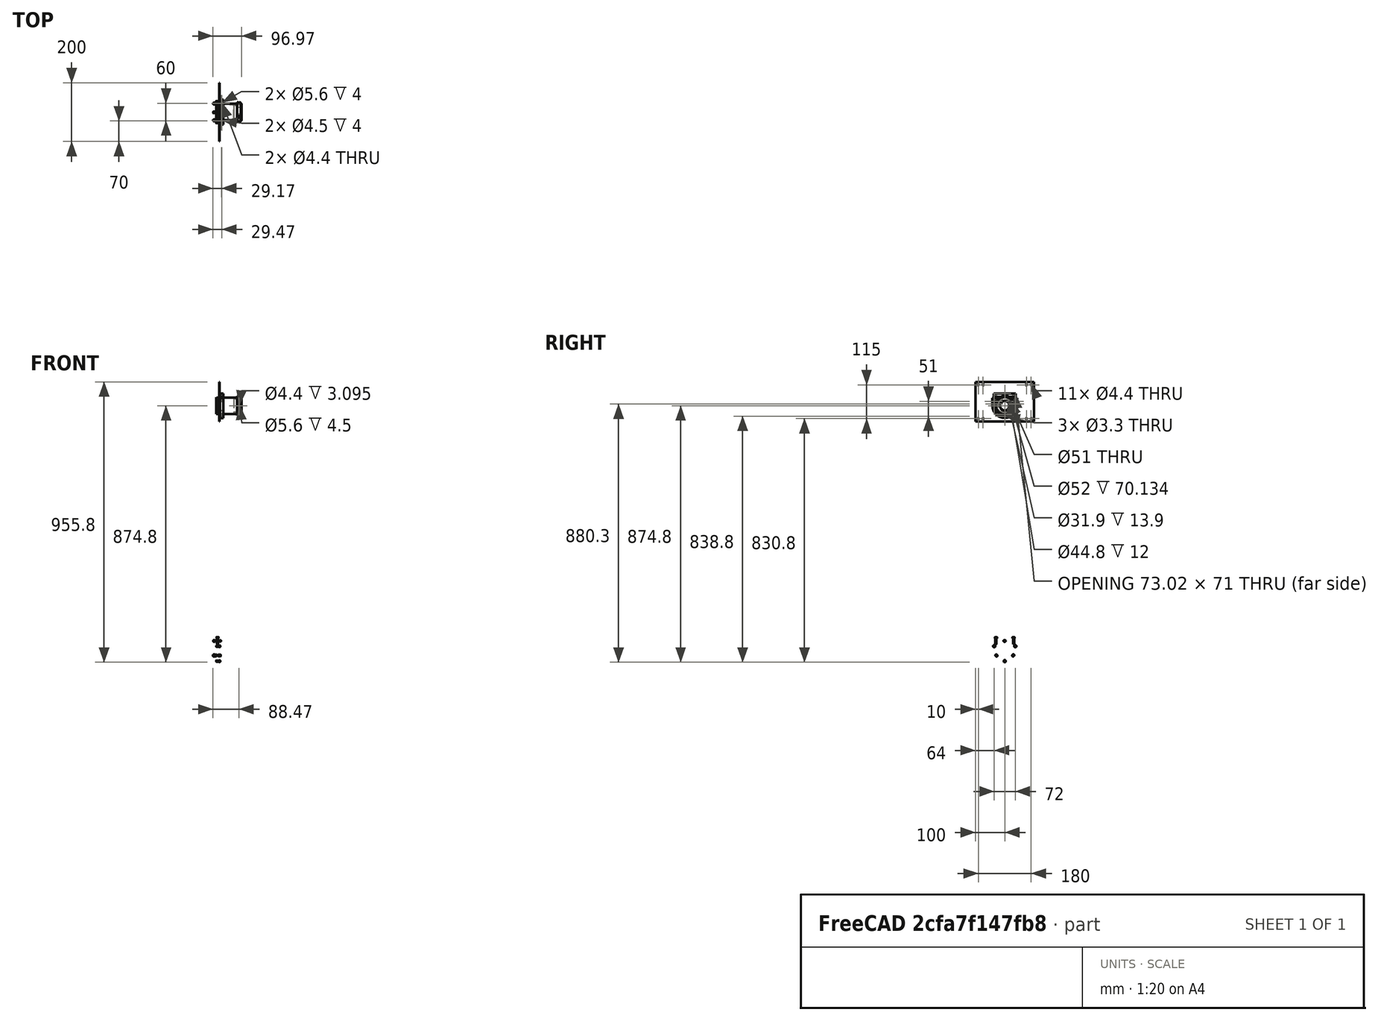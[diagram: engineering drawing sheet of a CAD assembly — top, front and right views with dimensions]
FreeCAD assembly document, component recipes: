
FREECAD ASSEMBLY — COMPONENT RECIPES ("Focuser")

This assembly document has 6 components, labeled P0..P5 below (a component is one placed body or linked part). 6 of them carry a construction recipe — the FreeCAD feature program that regenerates the part from scratch, quoted from this document or its linked companion documents; the rest are supplied as boundary geometry only. No exploded tour is included for this assembly.
COMPONENT P0 — recipe-attached ("FocuserTube", modeled in this document).
Construction recipe (the document's own serialized feature program — sketch geometry with constraints, then the solid features built on it; lengths are millimeters unless a unit is written):

FEATURE [Sketcher::SketchObject] Sketch022  label="Focuser_Profile"
  FullyConstrained = true
  MapMode = 5
  Support = -> [XY_Plane007]
  expr: Constraints[10] = <<Common>>#<<Parameters>>.foc_inner / 2
  expr: Constraints[11] = <<Common>>#<<Parameters>>.foc_flange
  expr: Constraints[16] = (<<Common>>#<<Parameters>>.foc_flangeinner + <<Common>>#<<Parameters>>.foc_itol) / 2
  expr: Constraints[18] = <<Common>>#<<Parameters>>.foc_shaft
  expr: Constraints[19] = <<Common>>#<<Parameters>>.foc_wall
  expr: Constraints[26] = <<Common>>#<<Parameters>>.foc_spacing / 2
  expr: Constraints[27] = <<Common>>#<<Parameters>>.foc_fheight
  sketch-geometry (12):
    g0: LineSegment StartX=0 StartY=26 StartZ=0 EndX=70.134 EndY=26 EndZ=0
    g1: LineSegment StartX=0 StartY=26 StartZ=0 EndX=0 EndY=29 EndZ=0
    g2: LineSegment StartX=2 StartY=28 StartZ=0 EndX=72 EndY=28 EndZ=0
    g3: LineSegment StartX=72 StartY=28 StartZ=0 EndX=72 EndY=33 EndZ=0
    g4: LineSegment StartX=72 StartY=33 StartZ=0 EndX=82 EndY=33 EndZ=0
    g5: LineSegment StartX=84 StartY=31 StartZ=0 EndX=84 EndY=25.5 EndZ=0
    g6: LineSegment StartX=70.134 StartY=26 StartZ=0 EndX=72 EndY=25.5 EndZ=0
    g7: LineSegment StartX=72 StartY=25.5 StartZ=0 EndX=84 EndY=25.5 EndZ=0
    g8: LineSegment StartX=0 StartY=29 StartZ=0 EndX=1 EndY=29 EndZ=0
    g9: LineSegment StartX=1 StartY=29 StartZ=0 EndX=2 EndY=28 EndZ=0
    g10: LineSegment StartX=72 StartY=28 StartZ=0 EndX=72 EndY=25.5 EndZ=0
    g11: ArcOfCircle CenterX=82 CenterY=31 CenterZ=0 NormalX=0 NormalY=0 NormalZ=1 AngleXU=0 Radius=2 StartAngle=4e-16 EndAngle=1.5708
  constraints (34):
    c: PointOnObject(g0,g-2)
    c: Horizontal(g0)
    c: Coincident(g1,g0)
    c: PointOnObject(g1,g-2)
    c: Horizontal(g2)
    c: Coincident(g3,g2)
    c: Vertical(g3)
    c: Coincident(g4,g3)
    c: Horizontal(g4)
    c: Vertical(g5)
    c: DistanceY(g-1,g0) = 26
    c: DistanceY(g0,g3) = 7
    c: Coincident(g6,g0)
    c: Coincident(g7,g6)
    c: Horizontal(g7)
    c: Coincident(g7,g5)
    c: DistanceY(g5) = 25.5
    c: Angle(g3,g6) = 1.309
    c: DistanceX(g1,g2) = 72
    c: DistanceY(g0,g2) = 2
    c: Coincident(g8,g1)
    c: Horizontal(g8)
    c: Coincident(g9,g8)
    c: Coincident(g9,g2)
    c: DistanceX(g8,g8) = 1
    c: Angle(g2,g9) = 2.35619
    c: DistanceY(g2,g1) = 1
    c: DistanceX(g6,g5) = 12
    c: Coincident(g10,g2)
    c: Coincident(g10,g6)
    c: Vertical(g10)
    c: Tangent(g4,g11) = 1.5708
    c: Tangent(g5,g11) = 1.5708
    c: Radius(g11) = 2
FEATURE [PartDesign::Revolution] Revolution001  label="Focuser_Shaft"
  Angle = 360
  Axis = (1,0,0)
  Base = (0,0,0)
  Profile = -> Sketch022
  ReferenceAxis = -> Sketch022 [H_Axis]
FEATURE [PartDesign::Plane] DatumPlane018  label="FocuserShaft_DatumPlane_Midpoint"
  AttachmentOffset = pos=(78,0,0) rot=(0,0,1;0rad)
  Length = 125.951
  MapMode = 5
  Placement = pos=(78,0,0) rot=(1,0,0;1.5708rad)
  ResizeMode = 0
  Support = -> [XZ_Plane007]
  Width = 82.8577
  expr: .AttachmentOffset.Base.x = <<Common>>#<<Parameters>>.foc_fheight / 2 + <<Common>>#<<Parameters>>.foc_shaft
FEATURE [Sketcher::SketchObject] Sketch031  label="FocuserShaft_Nut_Sketch"
  AttachmentOffset = pos=(0,0,33) rot=(0,0,1;0rad)
  FullyConstrained = true
  MapMode = 5
  Placement = pos=(78,33,7.3e-15) rot=(0,0.707107,0.707107;3.14159rad)
  Support = -> [DatumPlane018]
  expr: .AttachmentOffset.Base.z = <<Common>>#<<Parameters>>.foc_inner / 2 + <<Common>>#<<Parameters>>.foc_flange
  expr: Constraints[1] = <<Common>>#<<Parameters>>.acc_M4Bore
  sketch-geometry (1):
    g0: Circle CenterX=0 CenterY=0 CenterZ=0 NormalX=0 NormalY=0 NormalZ=1 AngleXU=0 Radius=2.8
  constraints (2):
    c: Coincident(g0,g-1)
    c: Diameter(g0) = 5.6
FEATURE [Sketcher::SketchObject] Sketch032  label="FocuserShaft_ScrewHole_Sketch"
  FullyConstrained = true
  MapMode = 5
  Placement = pos=(78,0,0) rot=(1,0,0;1.5708rad)
  Support = -> [DatumPlane018]
  sketch-geometry (1):
    g0: Circle CenterX=0 CenterY=0 CenterZ=0 NormalX=0 NormalY=0 NormalZ=1 AngleXU=0 Radius=2.2
  constraints (2):
    c: Coincident(g0,g-1)
    c: Diameter(g0) = 4.4
FEATURE [PartDesign::CoordinateSystem] Local_CS047  label="LCS_TubeBase"
  AttacherType = Attacher::AttachEngine3D
  MapMode = 11
  Placement = pos=(2,0,0) rot=(0.707107,0,0.707107;3.14159rad)
  Support = -> [Revolution001]
FEATURE [PartDesign::Plane] DatumPlane038  label="FocuserShaft_DatumPlane_AdaptorCut"
  AttachmentOffset = pos=(78,0,0) rot=(1,0,0;2.0944rad)
  Length = 128.821
  MapMode = 5
  Placement = pos=(78,0,0) rot=(1,0,0;3.66519rad)
  ResizeMode = 0
  Support = -> [XZ_Plane007]
  Width = 109.932
  expr: .AttachmentOffset.Base.x = <<Common>>#<<Parameters>>.foc_fheight / 2 + <<Common>>#<<Parameters>>.foc_shaft
FEATURE [Sketcher::SketchObject] Sketch146  label="FocuserShaft_AdaptorCut_Sketch"
  AttachmentOffset = pos=(0,0,-24.4) rot=(0,0,1;0rad)
  FullyConstrained = true
  MapMode = 5
  Placement = pos=(78,-12.2,21.131) rot=(1,0,0;3.66519rad)
  Support = -> [DatumPlane038]
  expr: .AttachmentOffset.Base.z = -(<<Common>>#<<Parameters>>.foc_flangeinner / 2) + 1
  expr: Constraints[13] = <<Common>>#<<Parameters>>.foc_fheight / 2 + 1
  expr: Constraints[5] = <<Common>>#<<Parameters>>.sec_sidebolt + 2
  sketch-geometry (5):
    g0: LineSegment StartX=7 StartY=3 StartZ=0 EndX=0 EndY=3 EndZ=0
    g1: LineSegment StartX=-6e-16 StartY=-3 StartZ=0 EndX=7 EndY=-3 EndZ=0
    g2: LineSegment StartX=7 StartY=-3 StartZ=0 EndX=7 EndY=3 EndZ=0
    g3: ArcOfCircle CenterX=0 CenterY=0 CenterZ=0 NormalX=0 NormalY=0 NormalZ=1 AngleXU=0 Radius=3 StartAngle=1.5708 EndAngle=4.71239
    g4: LineSegment StartX=-6e-16 StartY=3 StartZ=0 EndX=-6e-16 EndY=-3 EndZ=0
  constraints (15):
    c: Coincident(g1,g2)
    c: Coincident(g2,g0)
    c: Horizontal(g0)
    c: Horizontal(g1)
    c: Vertical(g2)
    c: DistanceY(g2,g2) = 6
    c: Symmetric(g0,g1,g-1)
    c: Coincident(g3,g0)
    c: Coincident(g3,g1)
    c: PointOnObject(g4,g0)
    c: Coincident(g4,g1)
    c: Vertical(g4)
    c: PointOnObject(g3,g4)
    c: DistanceX(g3,g0) = 7
    c: Coincident(g3,g-1)
FEATURE [PartDesign::CoordinateSystem] Local_CS229  label="LCS_TubeFlange"
  AttacherType = Attacher::AttachEngine3D
  MapMode = 11
  Placement = pos=(84,0,0) rot=(0.707107,0,0.707107;3.14159rad)
  Support = -> [Revolution001]
FEATURE [PartDesign::Pocket] Pocket195  label="FocuserShaft_Nut"
  BaseFeature = -> Revolution001
  Direction = (0,-1,-2e-16)
  Length = 4.5
  Length2 = 5
  Profile = -> Sketch031
  ReferenceAxis = -> Sketch031 [N_Axis]
  Type = 0
FEATURE [PartDesign::Pocket] Pocket196  label="FocuserShaft_ScrewHole"
  BaseFeature = -> Pocket195
  Direction = (0,1,2e-16)
  Length = 5
  Length2 = 5
  Profile = -> Sketch032
  ReferenceAxis = -> Sketch032 [N_Axis]
  Type = 1
FEATURE [PartDesign::PolarPattern] PolarPattern008  label="FocuserShaft_PolarPattern"
  Angle = 120
  Axis = -> X_Axis007
  BaseFeature = -> Pocket196
  Occurrences = 2
  Originals = -> [Pocket195,Pocket196]
  Reversed = true
FEATURE [PartDesign::CoordinateSystem] Local_CS048  label="LCS_TubeLock_Nut01"
  AttacherType = Attacher::AttachEngine3D
  AttachmentOffset = pos=(0,0,4) rot=(0,0,1;0rad)
  MapMode = 11
  Placement = pos=(78,32.5,6.8e-15) rot=(-0.57735,0.57735,0.57735;2.0944rad)
  Support = -> [PolarPattern008]
FEATURE [PartDesign::CoordinateSystem] Local_CS049  label="LCS_TubeLock_Nut02"
  AttacherType = Attacher::AttachEngine3D
  AttachmentOffset = pos=(0,0,4) rot=(0,0,1;0rad)
  MapMode = 11
  Placement = pos=(78,-16.25,-28.1458) rot=(0.694747,-0.694747,0.186157;2.77349rad)
  Support = -> [PolarPattern008]
FEATURE [PartDesign::CoordinateSystem] Local_CS050  label="LCS_TubeLock_Screw01"
  AttacherType = Attacher::AttachEngine3D
  AttachmentOffset = pos=(0,0,8) rot=(0,0,1;0rad)
  MapMode = 11
  Placement = pos=(78,36.5,7.2e-15) rot=(-0.57735,0.57735,0.57735;2.0944rad)
  Support = -> [PolarPattern008]
FEATURE [PartDesign::CoordinateSystem] Local_CS051  label="LCS_TubeLock_Screw02"
  AttacherType = Attacher::AttachEngine3D
  AttachmentOffset = pos=(0,0,8) rot=(0,0,1;0rad)
  MapMode = 11
  Placement = pos=(78,-18.25,-31.6099) rot=(0.694747,-0.694747,0.186157;2.77349rad)
  Support = -> [PolarPattern008]
FEATURE [PartDesign::Pocket] Pocket197  label="FocuserShaft_AdaptorCut"
  BaseFeature = -> PolarPattern008
  Direction = (0,-0.5,0.866025)
  Length = 5
  Length2 = 5
  Profile = -> Sketch146
  ReferenceAxis = -> Sketch146 [N_Axis]
  Type = 1
FEATURE [PartDesign::Chamfer] Chamfer001  label="FocuserShaft_RimChamfer"
  Angle = 45
  Base = -> Pocket197 [Edge14,Edge18]
  BaseFeature = -> Pocket197
  ChamferType = 0
  FlipDirection = false
  Size = 0.6
  Size2 = 1
  SupportTransform = false
  UseAllEdges = false
FEATURE [PartDesign::Body] Body007  label="FocuserTube"
  Group = -> [Sketch022,Revolution001,DatumPlane018,Sketch031,Sketch032,Local_CS047,Local_CS048,Local_CS049,Local_CS050,Local_CS051,DatumPlane038,Sketch146,Local_CS229,Pocket195,Pocket196,PolarPattern008,Pocket197,Chamfer001]
  Origin = -> Origin007
  Placement = pos=(110,0,835) rot=(0,0,1;0rad)
  Tip = -> Chamfer001
  expr: .Placement.Base.x = <<Common>>#<<Parameters>>.bolt_x + <<Common>>#<<Parameters>>.sec_poledia / 2 - <<Common>>#<<Parameters>>.foc_fheight
  expr: .Placement.Base.z = <<Common>>#<<Parameters>>.mirror_distance
COMPONENT P1 — recipe-attached ("FocuserSpring", modeled in this document).
Construction recipe (the document's own serialized feature program — sketch geometry with constraints, then the solid features built on it; lengths are millimeters unless a unit is written):

FEATURE [Sketcher::SketchObject] Sketch023  label="FocuserSpring_Base_Sketch"
  FullyConstrained = true
  MapMode = 5
  Placement = pos=(0,0,0) rot=(0.57735,0.57735,0.57735;2.0944rad)
  Support = -> [YZ_Plane008]
  expr: Constraints[13] = <<Common>>#<<Parameters>>.foc_clampblock
  expr: Constraints[2] = <<Common>>#<<Parameters>>.foc_baseflange
  expr: Constraints[3] = <<Common>>#<<Parameters>>.foc_inner / 2 + <<Common>>#<<Parameters>>.foc_wall + <<Common>>#<<Parameters>>.foc_spacing
  expr: Constraints[4] = <<Common>>#<<Parameters>>.foc_springblock
  expr: Constraints[9] = <<Common>>#<<Parameters>>.fbearing_outer + <<Common>>#<<Parameters>>.sec_fthick * 4
  sketch-geometry (6):
    g0: LineSegment StartX=38 StartY=42 StartZ=0 EndX=38 EndY=30 EndZ=0
    g1: LineSegment StartX=-38 StartY=30 StartZ=0 EndX=-38 EndY=42 EndZ=0
    g2: LineSegment StartX=-22 StartY=30 StartZ=0 EndX=22 EndY=30 EndZ=0
    g3: LineSegment StartX=-11 StartY=42 StartZ=0 EndX=11 EndY=42 EndZ=0
    g4: LineSegment StartX=-38 StartY=42 StartZ=0 EndX=38 EndY=42 EndZ=0
    g5: LineSegment StartX=-38 StartY=30 StartZ=0 EndX=38 EndY=30 EndZ=0
  constraints (17):
    c: Vertical(g0)
    c: Vertical(g1)
    c: DistanceY(g0,g0) = 12
    c: DistanceY(g-1,g0) = 30
    c: DistanceX(g1,g0) = 76
    c: Symmetric(g0,g1,g-2)
    c: Symmetric(g2,g2,g-2)
    c: Symmetric(g3,g3,g-2)
    c: Equal(g0,g1)
    c: DistanceX(g3,g3) = 22
    c: Coincident(g4,g1)
    c: Coincident(g4,g0)
    c: PointOnObject(g3,g4)
    c: DistanceX(g1,g2) = 16
    c: Coincident(g5,g1)
    c: Coincident(g5,g0)
    c: PointOnObject(g2,g5)
FEATURE [PartDesign::Pad] Pad007  label="FocuserSpring_Base"
  Direction = (1,-2e-16,3e-16)
  Length = 12
  Length2 = 100
  Placement = pos=(0,0,0) rot=(0.57735,0.57735,0.57735;2.0944rad)
  Profile = -> Sketch023
  Type = 0
  expr: Length = <<Common>>#<<Parameters>>.foc_fheight
FEATURE [Sketcher::SketchObject] Sketch065  label="FocuserSpring_Cut_Sketch"
  FullyConstrained = false
  MapMode = 5
  Support = -> [XY_Plane008]
  expr: Constraints[18] = <<Common>>#<<Parameters>>.fbearing_outer + <<Common>>#<<Parameters>>.sec_fthick
  expr: Constraints[1] = <<Common>>#<<Parameters>>.sec_sidebolt * 1.1
  expr: Constraints[28] = <<Common>>#<<Parameters>>.foc_fheight / 2
  expr: Constraints[2] = <<Common>>#<<Parameters>>.foc_springblock - <<Common>>#<<Parameters>>.foc_clampblock
  expr: Constraints[35] = <<Common>>#<<Parameters>>.fbearing_tilt
  expr: Constraints[4] = <<Common>>#<<Parameters>>.foc_fheight / 2
  sketch-geometry (14):
    g0: Circle CenterX=6 CenterY=30 CenterZ=0 NormalX=0 NormalY=0 NormalZ=1 AngleXU=0 Radius=2.2
    g1: Circle CenterX=6 CenterY=-30 CenterZ=0 NormalX=0 NormalY=0 NormalZ=1 AngleXU=0 Radius=2.2
    g2: GeomPoint X=6 Y=0 Z=0
    g3: LineSegment StartX=10.867 StartY=6.95063 StartZ=0 EndX=13 EndY=9.08366 EndZ=0
    g4: LineSegment StartX=13 StartY=9.08366 StartZ=0 EndX=13 EndY=-5.9999 EndZ=0
    g5: LineSegment StartX=13 StartY=-5.9999 StartZ=0 EndX=12 EndY=-5.9999 EndZ=0
    g6: LineSegment StartX=12 StartY=-5.9999 StartZ=0 EndX=10.867 EndY=6.95063 EndZ=0
    g7: LineSegment StartX=0 StartY=5.9999 StartZ=0 EndX=-1 EndY=5.9999 EndZ=0
    g8: LineSegment StartX=-1 StartY=5.9999 StartZ=0 EndX=-1 EndY=-9.08366 EndZ=0
    g9: LineSegment StartX=-1 StartY=-9.08366 StartZ=0 EndX=1.13302 EndY=-6.95063 EndZ=0
    g10: LineSegment StartX=1.13302 StartY=-6.95063 StartZ=0 EndX=0 EndY=5.9999 EndZ=0
    g11: LineSegment StartX=0.566512 StartY=-0.475369 StartZ=0 EndX=11.4335 EndY=0.475369 EndZ=0
    g12: GeomPoint X=0 Y=-8.08366 Z=0
    g13: GeomPoint X=12 Y=8.08366 Z=0
  constraints (36):
    c: Equal(g0,g1)
    c: Diameter(g1) = 4.4
    c: DistanceY(g1,g0) = 60
    c: Symmetric(g0,g1,g-1)
    c: DistanceX(g0) = 6
    c: Coincident(g3,g4)
    c: Coincident(g4,g5)
    c: Coincident(g5,g6)
    c: Coincident(g6,g3)
    c: Horizontal(g5)
    c: Vertical(g4)
    c: Coincident(g7,g8)
    c: Coincident(g8,g9)
    c: Coincident(g9,g10)
    c: Coincident(g10,g7)
    c: Horizontal(g7)
    c: Vertical(g8)
    c: Parallel(g9,g3)
    c: Distance(g6) = 13
    c: Equal(g6,g10)
    c: PointOnObject(g11,g10)
    c: PointOnObject(g11,g6)
    c: Symmetric(g5,g3,g11)
    c: Symmetric(g7,g9,g11)
    c: Equal(g7,g5)
    c: DistanceX(g5,g5) = 1
    c: PointOnObject(g2,g-1)
    c: PointOnObject(g2,g11)
    c: DistanceX(g-1,g2) = 6
    c: PointOnObject(g12,g9)
    c: PointOnObject(g13,g3)
    c: DistanceY(g12,g13) = 16.1673
    c: PointOnObject(g7,g-2)
    c: PointOnObject(g12,g-2)
    c: Angle(g9,g8) = 0.785398
    c: Angle(g-2,g10) = 0.0872665
FEATURE [PartDesign::Plane] DatumPlane008  label="FocuserSpring_DatumPlane_Shaft"
  AttachmentOffset = pos=(0,0,6) rot=(0,1,0;0.087266rad)
  Length = 94.7173
  MapMode = 2
  Placement = pos=(6,-1.3e-15,1.3e-15) rot=(0.543775,0.593426,0.593426;2.14549rad)
  ResizeMode = 0
  Support = -> [YZ_Plane008]
  Width = 81.6487
  expr: .AttachmentOffset.Base.z = <<Common>>#<<Parameters>>.foc_fheight / 2
  expr: .AttachmentOffset.Rotation.Pitch = <<Common>>#<<Parameters>>.fbearing_tilt
FEATURE [Sketcher::SketchObject] Sketch025  label="FocuserSpring_Shaft_Sketch"
  FullyConstrained = true
  MapMode = 5
  Placement = pos=(6,-1.4e-15,1.3e-15) rot=(0.543775,0.593426,0.593426;2.14549rad)
  Support = -> [DatumPlane008]
  expr: Constraints[0] = <<Common>>#<<Parameters>>.fbearing_inner * 1.1
  expr: Constraints[2] = <<Common>>#<<Parameters>>.foc_inner / 2 + <<Common>>#<<Parameters>>.foc_wall + <<Common>>#<<Parameters>>.fbearing_outer / 2
  sketch-geometry (1):
    g0: Circle CenterX=0 CenterY=33 CenterZ=0 NormalX=0 NormalY=0 NormalZ=1 AngleXU=0 Radius=1.65
  constraints (3):
    c: Diameter(g0) = 3.3
    c: PointOnObject(g0,g-2)
    c: DistanceY(g0) = 33
FEATURE [PartDesign::Pocket] Pocket021  label="FocuserSpring_Cut"
  BaseFeature = -> Pad007
  Direction = (0,0,-1)
  Length = 5
  Length2 = 100
  Midplane = true
  Placement = pos=(0,0,0) rot=(0.57735,0.57735,0.57735;2.0944rad)
  Profile = -> Sketch065
  Type = 1
FEATURE [PartDesign::Pocket] Pocket022  label="FocuserSpring_Shaft"
  BaseFeature = -> Pocket021
  Direction = (-0.996195,-0.0871557,-2e-16)
  Length = 5
  Length2 = 100
  Midplane = true
  Placement = pos=(0,0,0) rot=(0.57735,0.57735,0.57735;2.0944rad)
  Profile = -> Sketch025
  Type = 1
FEATURE [PartDesign::CoordinateSystem] Local_CS041  label="LCS_SpringBase_A"
  AttacherType = Attacher::AttachEngine3D
  MapMode = 11
  Placement = pos=(6,30,30) rot=(0,0,1;1.5708rad)
  Support = -> [Pocket022]
FEATURE [PartDesign::CoordinateSystem] Local_CS134  label="LCS_SpringBase_F"
  AttacherType = Attacher::AttachEngine3D
  MapMode = 11
  Placement = pos=(6,-30,30) rot=(0,0,1;1.5708rad)
  Support = -> [Pocket022]
FEATURE [PartDesign::CoordinateSystem] Local_CS043  label="LCS_SpringBolt_A"
  AttacherType = Attacher::AttachEngine3D
  MapMode = 11
  Placement = pos=(6,30,42) rot=(0,0,1;1.5708rad)
  Support = -> [Pocket022]
FEATURE [PartDesign::CoordinateSystem] Local_CS135  label="LCS_SpringBolt_F"
  AttacherType = Attacher::AttachEngine3D
  MapMode = 11
  Placement = pos=(6,-30,42) rot=(0,0,1;1.5708rad)
  Support = -> [Pocket022]
FEATURE [PartDesign::CoordinateSystem] Local_CS045  label="LCS_Bearing_Inner_Z"
  AttacherType = Attacher::AttachEngine3D
  MapMode = 11
  Placement = pos=(0.566512,-0.475369,33) rot=(0.70677,0.030858,-0.70677;3.0799rad)
  Support = -> [Pocket022]
FEATURE [PartDesign::CoordinateSystem] Local_CS046  label="LCS_Bearing_Outer_Z"
  AttacherType = Attacher::AttachEngine3D
  MapMode = 11
  Placement = pos=(11.4335,0.475369,33) rot=(0.70677,0.030858,0.70677;3.20329rad)
  Support = -> [Pocket022]
FEATURE [PartDesign::Chamfer] Chamfer004
  Angle = 45
  Base = -> Pocket022 [Face3,Face2]
  BaseFeature = -> Pocket022
  ChamferType = 0
  FlipDirection = false
  Placement = pos=(0,0,0) rot=(0.57735,0.57735,0.57735;2.0944rad)
  Size = 0.4
  Size2 = 1
  SupportTransform = false
  UseAllEdges = false
FEATURE [PartDesign::Body] Body008  label="FocuserSpring"
  Group = -> [Sketch023,Pad007,Sketch065,Pocket021,DatumPlane008,Sketch025,Pocket022,Local_CS041,Local_CS134,Local_CS043,Local_CS135,Local_CS045,Local_CS046,Chamfer004]
  Origin = -> Origin008
  Placement = pos=(122.7,0,835) rot=(0,0,1;0rad)
  Tip = -> Chamfer004
  expr: .Placement.Base.x = <<Common>>#<<Parameters>>.bolt_x + <<Common>>#<<Parameters>>.sec_poledia / 2 + <<Common>>#<<Parameters>>.sec_clamptol
  expr: .Placement.Base.z = <<Common>>#<<Parameters>>.mirror_distance
COMPONENT P2 — recipe-attached ("FocuserBase", modeled in this document).
Construction recipe (the document's own serialized feature program — sketch geometry with constraints, then the solid features built on it; lengths are millimeters unless a unit is written):

FEATURE [Sketcher::SketchObject] Sketch021  label="FocuserBase_Ring_Sketch"
  FullyConstrained = true
  MapMode = 5
  Placement = pos=(0,0,0) rot=(0.57735,0.57735,0.57735;2.0944rad)
  Support = -> [YZ_Plane057]
  expr: .Constraints.flange_inner = <<Common>>#<<Parameters>>.foc_inner / 2 + <<Common>>#<<Parameters>>.foc_wall + <<Common>>#<<Parameters>>.foc_spacing
  expr: .Constraints.flange_outer = .Constraints.flange_inner + <<Common>>#<<Parameters>>.foc_baseflange * 1 mm
  expr: Constraints[20] = <<Common>>#<<Parameters>>.foc_fthick * 1.5
  expr: Constraints[26] = max(<<Common>>#<<Parameters>>.foc_springblock * 1 mm; .Constraints.flange_outer * 2)
  expr: Constraints[30] = <<Common>>#<<Parameters>>.sec_fthick * 2
  sketch-geometry (14):
    g0: Circle CenterX=0 CenterY=0 CenterZ=0 NormalX=0 NormalY=0 NormalZ=1 AngleXU=0 Radius=30
    g1: Circle CenterX=0 CenterY=0 CenterZ=0 NormalX=0 NormalY=0 NormalZ=1 AngleXU=0 Radius=42
    g2: LineSegment StartX=0 StartY=0 StartZ=0 EndX=36.3731 EndY=-21 EndZ=0
    g3: LineSegment StartX=0 StartY=0 StartZ=0 EndX=-36.3731 EndY=-21 EndZ=0
    g4: LineSegment StartX=-42 StartY=26.25 StartZ=0 EndX=-22.1345 EndY=26.25 EndZ=0
    g5: LineSegment StartX=22.1345 StartY=26.25 StartZ=0 EndX=42 EndY=26.25 EndZ=0
    g6: LineSegment StartX=-42 StartY=26.25 StartZ=0 EndX=-42 EndY=8.27963e-05 EndZ=0
    g7: LineSegment StartX=-22.1345 StartY=26.25 StartZ=0 EndX=-22.1345 EndY=20.25 EndZ=0
    g8: LineSegment StartX=22.1345 StartY=26.25 StartZ=0 EndX=22.1345 EndY=20.25 EndZ=0
    g9: LineSegment StartX=42 StartY=26.25 StartZ=0 EndX=42 EndY=8.27947e-05 EndZ=0
    g10: GeomPoint X=0 Y=30 Z=0
    g11: ArcOfCircle CenterX=0 CenterY=0 CenterZ=0 NormalX=0 NormalY=0 NormalZ=1 AngleXU=0 Radius=30 StartAngle=2.40063 EndAngle=7.02415
    g12: ArcOfCircle CenterX=0 CenterY=0 CenterZ=0 NormalX=0 NormalY=0 NormalZ=1 AngleXU=0 Radius=42 StartAngle=3.14159 EndAngle=4.71239
    g13: ArcOfCircle CenterX=0 CenterY=0 CenterZ=0 NormalX=0 NormalY=0 NormalZ=1 AngleXU=0 Radius=42 StartAngle=4.71239 EndAngle=6.28319
  constraints (37):
    c: Coincident(g0,g-1)
    c: Coincident(g1,g0)
    c: Radius(g0) = 30  'flange_inner'
    c: Radius(g1) = 42  'flange_outer'
    c: Coincident(g2,g0)
    c: Coincident(g3,g0)
    c: PointOnObject(g2,g1)
    c: Angle(g3,g2) = 2.0944
    c: Horizontal(g4)
    c: Horizontal(g5)
    c: Coincident(g6,g4)
    c: Coincident(g7,g4)
    c: Vertical(g7)
    c: Coincident(g8,g5)
    c: Vertical(g8)
    c: Coincident(g9,g5)
    c: Symmetric(g4,g5,g-2)
    c: Equal(g4,g5)
    c: PointOnObject(g10,g0)
    c: PointOnObject(g10,g-2)
    c: DistanceY(g4,g10) = 3.75
    c: Coincident(g11,g-1)
    c: Coincident(g12,g11)
    c: Coincident(g12,g6)
    c: Coincident(g13,g11)
    c: Coincident(g13,g9)
    c: DistanceX(g4,g5) = 84
    c: Equal(g12,g1)
    c: Tangent(g6,g12)
    c: Tangent(g9,g13)
    c: DistanceY(g7,g7) = 6
    c: Coincident(g11,g7)
    c: Coincident(g11,g8)
    c: PointOnObject(g7,g0)
    c: Coincident(g13,g12)
    c: PointOnObject(g12,g-2)
    c: Symmetric(g3,g2,g-2)
FEATURE [PartDesign::Pad] Pad006  label="FocuserBase_Ring"
  Direction = (1,-2e-16,3e-16)
  Length = 12
  Length2 = 100
  Placement = pos=(0,0,0) rot=(0.57735,0.57735,0.57735;2.0944rad)
  Profile = -> Sketch021
  Type = 0
  expr: Length = <<Common>>#<<Parameters>>.foc_fheight
FEATURE [PartDesign::Plane] DatumPlane015  label="FocuserBase_DatumPlane_SideCut"
  AttachmentOffset = pos=(6,28.5788,-16.5) rot=(1,0,0;1.0472rad)
  Length = 64.2201
  MapMode = 2
  Placement = pos=(6,28.5788,-16.5) rot=(1,0,0;1.0472rad)
  ResizeMode = 0
  Support = -> [XY_Plane057]
  Width = 115.326
  expr: .AttachmentOffset.Base.x = <<Common>>#<<Parameters>>.foc_fheight / 2
  expr: .AttachmentOffset.Base.y = (<<Common>>#<<Parameters>>.foc_inner / 2 + <<Common>>#<<Parameters>>.foc_wall + <<Common>>#<<Parameters>>.fbearing_outer / 2) * sin(60)
  expr: .AttachmentOffset.Base.z = -(<<Common>>#<<Parameters>>.foc_inner / 2 + <<Common>>#<<Parameters>>.foc_wall + <<Common>>#<<Parameters>>.fbearing_outer / 2) * cos(60)
FEATURE [PartDesign::Plane] DatumPlane016  label="FocuserBase_DatumPlane_SideShaft"
  AttachmentOffset = pos=(0,0,0) rot=(0,-1,0;0.087266rad)
  Length = 126.274
  MapMode = 4
  Placement = pos=(6,28.5788,-16.5) rot=(0.725486,0.178129,0.664786;2.75759rad)
  ResizeMode = 0
  Support = -> [DatumPlane015]
  Width = 128.065
  expr: .AttachmentOffset.Rotation.Pitch = -<<Common>>#<<Parameters>>.fbearing_tilt
FEATURE [PartDesign::Plane] DatumPlane011  label="FocuserBase_DatumPlane_SpringShaft"
  AttachmentOffset = pos=(6,0,26.25) rot=(0,0,1;0rad)
  Length = 62.9615
  MapMode = 5
  Placement = pos=(6,0,26.25) rot=(0,0,1;0rad)
  ResizeMode = 0
  Support = -> [XY_Plane057]
  Width = 96.9615
  expr: .AttachmentOffset.Base.x = <<Common>>#<<Parameters>>.foc_fheight / 2
  expr: .AttachmentOffset.Base.z = <<Common>>#<<Parameters>>.foc_inner / 2 + <<Common>>#<<Parameters>>.foc_wall + <<Common>>#<<Parameters>>.foc_spacing - <<Common>>#<<Parameters>>.foc_fthick * 1.5
FEATURE [Sketcher::SketchObject] Sketch067  label="FocuserBase_SpringShaft_Sketch"
  FullyConstrained = true
  MapMode = 5
  Placement = pos=(6,0,26.25) rot=(0,0,1;0rad)
  Support = -> [DatumPlane011]
  expr: Constraints[0] = <<Common>>#<<Parameters>>.sec_sidebolt * 1.1
  expr: Constraints[3] = <<Common>>#<<Parameters>>.foc_springblock - <<Common>>#<<Parameters>>.foc_clampblock
  sketch-geometry (2):
    g0: Circle CenterX=0 CenterY=30 CenterZ=0 NormalX=0 NormalY=0 NormalZ=1 AngleXU=0 Radius=2.2
    g1: Circle CenterX=0 CenterY=-30 CenterZ=0 NormalX=0 NormalY=0 NormalZ=1 AngleXU=0 Radius=2.2
  constraints (5):
    c: Diameter(g1) = 4.4
    c: Equal(g1,g0)
    c: Symmetric(g1,g0,g-1)
    c: DistanceY(g1,g0) = 60
    c: PointOnObject(g0,g-2)
FEATURE [PartDesign::Plane] DatumPlane017  label="FocuserBase_DatumPlane_FrontFace"
  AttachmentOffset = pos=(0,0,12) rot=(0,0,1;0rad)
  Length = 99.1433
  MapMode = 5
  Placement = pos=(12,-2.7e-15,2.7e-15) rot=(0.57735,0.57735,0.57735;2.0944rad)
  ResizeMode = 0
  Support = -> [YZ_Plane057]
  Width = 83.3933
  expr: .AttachmentOffset.Base.z = <<Common>>#<<Parameters>>.foc_fheight
FEATURE [PartDesign::CoordinateSystem] Local_CS130  label="LCS_TubeDatum"
  AttacherType = Attacher::AttachEngine3D
  AttachmentOffset = pos=(0,0,-12) rot=(0,0,1;0rad)
  MapMode = 5
  Placement = pos=(-12,2.7e-15,-2.7e-15) rot=(0.57735,0.57735,0.57735;2.0944rad)
  Support = -> [YZ_Plane057]
  expr: .AttachmentOffset.Base.z = -<<Common>>#<<Parameters>>.foc_fheight
FEATURE [Sketcher::SketchObject] Sketch077  label="FocuserBase_MountHoles_Sketch"
  FullyConstrained = true
  MapMode = 5
  Placement = pos=(12,-2.7e-15,2.7e-15) rot=(0.57735,0.57735,0.57735;2.0944rad)
  Support = -> [DatumPlane017]
  expr: Constraints[2] = <<Common>>#<<Parameters>>.sec_collbolt
  expr: Constraints[5] = <<Common>>#<<Parameters>>.foc_mbrad
  expr: Constraints[6] = <<Common>>#<<Parameters>>.foc_mbrad - <<Common>>#<<Parameters>>.foc_baseflange / 2 - <<Common>>#<<Parameters>>.sec_fthick - <<Common>>#<<Parameters>>.sec_sidebolt * 3
  expr: Constraints[7] = <<Common>>#<<Parameters>>.foc_mbrad
  sketch-geometry (3):
    g0: Circle CenterX=0 CenterY=-36 CenterZ=0 NormalX=0 NormalY=0 NormalZ=1 AngleXU=0 Radius=2
    g1: Circle CenterX=-36 CenterY=15 CenterZ=0 NormalX=0 NormalY=0 NormalZ=1 AngleXU=0 Radius=2
    g2: Circle CenterX=36 CenterY=15 CenterZ=0 NormalX=0 NormalY=0 NormalZ=1 AngleXU=0 Radius=2
  constraints (8):
    c: Symmetric(g1,g2,g-2)
    c: PointOnObject(g0,g-2)
    c: Diameter(g0) = 4
    c: Equal(g0,g1)
    c: Equal(g0,g2)
    c: DistanceY(g0,g-1) = 36
    c: DistanceY(g2) = 15
    c: DistanceX(g2) = 36
FEATURE [PartDesign::CoordinateSystem] Local_CS137  label="LCS_FocuserBase_MountN"
  AttacherType = Attacher::AttachEngine3D
  AttachmentOffset = pos=(0,-36,0) rot=(0,0,1;1.5708rad)
  MapMode = 5
  Placement = pos=(12,-6.7e-15,-36) rot=(0.707107,0,0.707107;3.14159rad)
  Support = -> [DatumPlane017]
  expr: .AttachmentOffset.Base.y = -<<Common>>#<<Parameters>>.foc_mbrad
FEATURE [PartDesign::Plane] DatumPlane027  label="FocuserBase_DatumPlane_NutCut"
  AttachmentOffset = pos=(0,0,-3) rot=(0,0,1;0rad)
  Length = 62.9615
  MapMode = 2
  Placement = pos=(6,0,23.25) rot=(0,0,1;0rad)
  ResizeMode = 0
  Support = -> [DatumPlane011]
  Width = 96.9615
  expr: .AttachmentOffset.Base.z = -<<Common>>#<<Parameters>>.sec_fthick
FEATURE [PartDesign::Line] DatumLine002  label="FocuserBase_DatumLine_SideShaft"
  AttacherType = Attacher::AttachEngineLine
  Length = 20
  MapMode = 18
  Placement = pos=(6,28.5788,-16.5) rot=(0.725486,0.178129,0.664786;2.75759rad)
  ResizeMode = 0
  Support = -> [DatumPlane016]
FEATURE [Sketcher::SketchObject] Sketch066  label="FocuserBase_SideCut_Sketch"
  ExternalGeometry = -> [Pad006,DatumLine002]
  FullyConstrained = true
  MapMode = 5
  Placement = pos=(6,28.5788,-16.5) rot=(1,0,0;1.0472rad)
  Support = -> [DatumPlane015]
  expr: Constraints[37] = (<<Common>>#<<Parameters>>.fbearing_outer + <<Common>>#<<Parameters>>.foc_fthick) / 2
  expr: Constraints[38] = <<Common>>#<<Parameters>>.fbearing_inner / 2
  sketch-geometry (21):
    g0: LineSegment StartX=-6.4 StartY=8.92025 StartZ=0 EndX=-7.12588 EndY=0.623433 EndZ=0
    g1: LineSegment StartX=5.6 StartY=5.78394 StartZ=0 EndX=7.85175 EndY=7.67338 EndZ=0
    g2: LineSegment StartX=7.85175 StartY=7.67338 StartZ=0 EndX=7.12588 EndY=-0.623433 EndZ=0
    g3: LineSegment StartX=-4.51055 StartY=6.6685 StartZ=0 EndX=5.6 EndY=5.78394 EndZ=0
    g4: LineSegment StartX=-6.4 StartY=8.92025 StartZ=0 EndX=-4.51055 EndY=6.6685 EndZ=0
    g5: LineSegment StartX=-4.92454 StartY=1.93657 StartZ=0 EndX=-4.51055 EndY=6.6685 EndZ=0
    g6: LineSegment StartX=5.18601 StartY=1.05201 StartZ=0 EndX=5.6 EndY=5.78394 EndZ=0
    g7: LineSegment StartX=4.51055 StartY=-6.6685 StartZ=0 EndX=6.4 EndY=-8.92025 EndZ=0
    g8: LineSegment StartX=-5.6 StartY=-5.78394 StartZ=0 EndX=4.51055 EndY=-6.6685 EndZ=0
    g9: LineSegment StartX=-4.92454 StartY=1.93657 StartZ=0 EndX=5.18601 EndY=1.05201 EndZ=0
    g10: LineSegment StartX=-7.12588 StartY=0.623433 StartZ=0 EndX=7.12588 EndY=-0.623433 EndZ=0
    g11: LineSegment StartX=-5.05528 StartY=0.442279 StartZ=0 EndX=-5.6 EndY=-5.78394 EndZ=0
    g12: LineSegment StartX=-5.05528 StartY=0.442279 StartZ=0 EndX=-4.92454 EndY=1.93657 EndZ=0
    g13: LineSegment StartX=7.12588 StartY=-0.623433 StartZ=0 EndX=6.4 EndY=-8.92025 EndZ=0
    g14: LineSegment StartX=-7.12588 StartY=0.623433 StartZ=0 EndX=-7.85175 EndY=-7.67338 EndZ=0
    g15: LineSegment StartX=-7.85175 StartY=-7.67338 StartZ=0 EndX=-5.6 EndY=-5.78394 EndZ=0
    g16: LineSegment StartX=5.6 StartY=5.78394 StartZ=0 EndX=6 EndY=5.78394 EndZ=0
    g17: LineSegment StartX=-6.4 StartY=8.92025 StartZ=0 EndX=-6 EndY=8.92025 EndZ=0
    g18: LineSegment StartX=-6 StartY=-5.78394 StartZ=0 EndX=-5.6 EndY=-5.78394 EndZ=0
    g19: LineSegment StartX=6.4 StartY=-8.92025 StartZ=0 EndX=6 EndY=-8.92025 EndZ=0
    g20: LineSegment StartX=5.18601 StartY=1.05201 StartZ=0 EndX=4.51055 EndY=-6.6685 EndZ=0
  constraints (59):
    c: Coincident(g4,g0)
    c: Parallel(g3,g-5)
    c: Coincident(g5,g4)
    c: Coincident(g5,g3)
    c: Coincident(g6,g1)
    c: Coincident(g6,g3)
    c: Coincident(g1,g2)
    c: Parallel(g5,g0)
    c: Parallel(g6,g2)
    c: Angle(g4,g5) = 2.35619
    c: Parallel(g8,g-5)
    c: Perpendicular(g-5,g0)
    c: Angle(g6,g1) = 2.35619
    c: Parallel(g5,g6)
    c: Equal(g5,g6)
    c: Coincident(g9,g5)
    c: Coincident(g9,g6)
    c: Coincident(g10,g0)
    c: Coincident(g10,g2)
    c: PointOnObject(g0,g-5)
    c: PointOnObject(g2,g-5)
    c: PointOnObject(g11,g10)
    c: Coincident(g11,g8)
    c: Coincident(g12,g11)
    c: Coincident(g12,g5)
    c: Coincident(g13,g2)
    c: Coincident(g13,g7)
    c: Coincident(g7,g8)
    c: PointOnObject(g11,g5)
    c: Equal(g13,g2)
    c: Equal(g2,g0)
    c: Coincident(g14,g0)
    c: Coincident(g15,g14)
    c: Coincident(g15,g8)
    c: PointOnObject(g14,g0)
    c: Parallel(g15,g1)
    c: Parallel(g7,g4)
    c: Distance(g11) = 6.25
    c: Distance(g12) = 1.5
    c: Coincident(g16,g1)
    c: PointOnObject(g16,g-3)
    c: Horizontal(g16)
    c: Coincident(g17,g0)
    c: PointOnObject(g17,g-4)
    c: Horizontal(g17)
    c: PointOnObject(g18,g-4)
    c: Coincident(g18,g8)
    c: Horizontal(g18)
    c: Coincident(g19,g7)
    c: PointOnObject(g19,g-3)
    c: Horizontal(g19)
    c: Equal(g19,g16)
    c: Equal(g16,g17)
    c: Equal(g17,g18)
    c: Parallel(g11,g12)
    c: Coincident(g20,g6)
    c: Coincident(g20,g7)
    c: Parallel(g20,g6)
    c: DistanceX(g17,g17) = 0.4
FEATURE [PartDesign::Groove] Groove  label="FocuserBase_SideCut"
  Angle = 360
  Axis = (0.996195,-0.0435779,-0.0754791)
  Base = (6,28.5788,-16.5)
  BaseFeature = -> Pad006
  Placement = pos=(0,0,0) rot=(0.57735,0.57735,0.57735;2.0944rad)
  Profile = -> Sketch066
  ReferenceAxis = -> DatumLine002
FEATURE [PartDesign::PolarPattern] PolarPattern  label="FocuserBase_PolarPattern"
  Angle = 360
  Axis = -> X_Axis057
  BaseFeature = -> Groove
  Occurrences = 3
  Originals = -> [Groove]
  Placement = pos=(0,0,0) rot=(0.57735,0.57735,0.57735;2.0944rad)
FEATURE [PartDesign::CoordinateSystem] Local_CS033  label="LCS_Bearing_Inner_NF"
  AttacherType = Attacher::AttachEngine3D
  MapMode = 11
  Placement = pos=(0.944723,-28.3577,-16.883) rot=(0.663579,-0.401957,-0.630947;2.47638rad)
  Support = -> [PolarPattern]
FEATURE [PartDesign::CoordinateSystem] Local_CS034  label="LCS_Bearing_Inner_NA"
  AttacherType = Attacher::AttachEngine3D
  MapMode = 11
  Placement = pos=(0.944723,28.8,-16.117) rot=(-0.644711,-0.352973,0.678055;2.36216rad)
  Support = -> [PolarPattern]
FEATURE [PartDesign::CoordinateSystem] Local_CS035  label="LCS_Bearing_Outer_NF"
  AttacherType = Attacher::AttachEngine3D
  MapMode = 11
  Placement = pos=(11.0553,-28.8,-16.117) rot=(0.644711,0.352973,0.678055;2.36216rad)
  Support = -> [PolarPattern]
FEATURE [PartDesign::CoordinateSystem] Local_CS036  label="LCS_Bearing_Outer_NA"
  AttacherType = Attacher::AttachEngine3D
  MapMode = 11
  Placement = pos=(11.0553,28.3577,-16.883) rot=(0.663579,-0.401957,0.630947;3.8068rad)
  Support = -> [PolarPattern]
FEATURE [PartDesign::Hole] Hole  label="FocuserBase_SpringShaft"
  BaseFeature = -> PolarPattern
  CustomThreadClearance = 0
  Depth = 8
  DepthType = 0
  Diameter = 4.5
  DrillForDepth = false
  DrillPoint = 1
  DrillPointAngle = 118
  HoleCutCountersinkAngle = 90
  HoleCutCustomValues = false
  HoleCutDepth = 4
  HoleCutDiameter = 5.6
  HoleCutType = 1
  ModelThread = false
  Placement = pos=(0,0,0) rot=(0.57735,0.57735,0.57735;2.0944rad)
  Profile = -> Sketch067
  Tapered = false
  TaperedAngle = 90
  ThreadClass = 0
  ThreadDepth = 8
  ThreadDepthType = 0
  ThreadDirection = 0
  ThreadFit = 0
  ThreadSize = 11
  ThreadType = 1
  Threaded = false
  UseCustomThreadClearance = false
  expr: HoleCutDiameter = Common#<<Parameters>>.acc_M4Bore
FEATURE [PartDesign::CoordinateSystem] Local_CS037  label="LCS_SpringNut_F"
  AttacherType = Attacher::AttachEngine3D
  MapMode = 11
  Placement = pos=(6,-30,26.25) rot=(0,0,1;3.14159rad)
  Support = -> [Hole]
FEATURE [PartDesign::CoordinateSystem] Local_CS038  label="LCS_SpringNut_A"
  AttacherType = Attacher::AttachEngine3D
  MapMode = 11
  Placement = pos=(6,30,26.25) rot=(0,0,1;3.14159rad)
  Support = -> [Hole]
FEATURE [PartDesign::CoordinateSystem] Local_CS132  label="LCS_SpringAttachment_F"
  AttacherType = Attacher::AttachEngine3D
  AttachmentOffset = pos=(0,0,3.75) rot=(0,0,1;0rad)
  MapMode = 11
  Placement = pos=(6,-30,30) rot=(0,0,1;3.14159rad)
  Support = -> [Hole]
  expr: .AttachmentOffset.Base.z = <<Common>>#<<Parameters>>.foc_fthick * 1.5
FEATURE [PartDesign::CoordinateSystem] Local_CS133  label="LCS_SpringAttachment_A"
  AttacherType = Attacher::AttachEngine3D
  AttachmentOffset = pos=(0,0,3.75) rot=(0,0,1;0rad)
  MapMode = 11
  Placement = pos=(6,30,30) rot=(0,0,1;3.14159rad)
  Support = -> [Hole]
  expr: .AttachmentOffset.Base.z = <<Common>>#<<Parameters>>.foc_fthick * 1.5
FEATURE [PartDesign::Hole] Hole051  label="FocuserBase_MountHoles"
  BaseFeature = -> Hole
  CustomThreadClearance = 0
  Depth = 219.967
  DepthType = 1
  Diameter = 3.3
  DrillForDepth = false
  DrillPoint = 1
  DrillPointAngle = 118
  HoleCutCountersinkAngle = 90
  HoleCutCustomValues = false
  HoleCutDepth = 0
  HoleCutDiameter = 6.1
  HoleCutType = 0
  ModelThread = false
  Placement = pos=(0,0,0) rot=(0.57735,0.57735,0.57735;2.0944rad)
  Profile = -> Sketch077
  Tapered = false
  TaperedAngle = 90
  ThreadClass = 0
  ThreadDepth = 219.967
  ThreadDepthType = 0
  ThreadDirection = 0
  ThreadFit = 0
  ThreadSize = 11
  ThreadType = 1
  Threaded = true
  UseCustomThreadClearance = false
FEATURE [PartDesign::Chamfer] Chamfer  label="FocuserBase_Chamfer"
  Angle = 45
  Base = -> Hole051 [Face5,Face4]
  BaseFeature = -> Hole051
  ChamferType = 0
  FlipDirection = false
  Placement = pos=(0,0,0) rot=(0.57735,0.57735,0.57735;2.0944rad)
  Size = 0.4
  Size2 = 1
  SupportTransform = false
  UseAllEdges = false
FEATURE [PartDesign::Body] Body022004  label="FocuserBase"
  Group = -> [Sketch021,Pad006,DatumPlane015,Sketch066,DatumPlane016,DatumPlane011,Sketch067,DatumPlane017,Local_CS130,Local_CS033,Local_CS034,Local_CS035,Local_CS036,Local_CS037,Local_CS038,Local_CS132,Local_CS133,Sketch077,Local_CS137,DatumPlane027,DatumLine002,Groove,PolarPattern,Hole,Hole051,Chamfer]
  Origin = -> Origin057
  Placement = pos=(123,0,835) rot=(0,0,1;0rad)
  Tip = -> Chamfer
  expr: .Placement.Base.x = <<Common>>#<<Parameters>>.bolt_x + <<Common>>#<<Parameters>>.sec_poledia / 2 + <<Common>>#<<Parameters>>.sec_spthick
  expr: .Placement.Base.z = <<Common>>#<<Parameters>>.mirror_distance
COMPONENT P3 — recipe-attached ("FocuserPlate", modeled in this document).
Construction recipe (the document's own serialized feature program — sketch geometry with constraints, then the solid features built on it; lengths are millimeters unless a unit is written):

FEATURE [Sketcher::SketchObject] Sketch078  label="FocuserPlate_Sketch"
  FullyConstrained = true
  MapMode = 5
  Placement = pos=(0,0,0) rot=(0.57735,0.57735,0.57735;2.0944rad)
  Support = -> [YZ_Plane014]
  expr: Constraints[106] = <<Common>>#<<Parameters>>.sec_sidebolt_y
  expr: Constraints[107] = <<Common>>#<<Parameters>>.sec_sidebolt * 4
  expr: Constraints[111] = <<Common>>#<<Parameters>>.sec_sidebolt * 1.1
  expr: Constraints[11] = <<Common>>#<<Parameters>>.foc_inner / 2 + <<Common>>#<<Parameters>>.foc_wall + <<Common>>#<<Parameters>>.foc_spacing
  expr: Constraints[12] = -(<<Common>>#<<Parameters>>.sec_sidebolt_lower_z - <<Common>>#<<Parameters>>.mirror_distance) + <<Common>>#<<Parameters>>.sec_clampheight / 2
  expr: Constraints[151] = <<Common>>#<<Parameters>>.sec_sidebolt * 1.1
  expr: Constraints[153] = <<Common>>#<<Parameters>>.sec_mtvar
  expr: Constraints[18] = <<Common>>#<<Parameters>>.foc_inner / 2 + <<Common>>#<<Parameters>>.foc_wall + <<Common>>#<<Parameters>>.fbearing_outer / 2
  expr: Constraints[50] = <<Common>>#<<Parameters>>.fbearing_outer + <<Common>>#<<Parameters>>.sec_fthick * 2
  expr: Constraints[58] = <<Common>>#<<Parameters>>.fbearing_outer / 2 + <<Common>>#<<Parameters>>.sec_fthick
  expr: Constraints[78] = <<Common>>#<<Parameters>>.sec_sidebolt * 1.1
  expr: Constraints[89] = <<Common>>#<<Parameters>>.foc_mbrad
  expr: Constraints[8] = <<Common>>#<<Parameters>>.bolt_y - <<Common>>#<<Parameters>>.pri_poledia / 2 - <<Common>>#<<Parameters>>.sec_fthick
  expr: Constraints[90] = <<Common>>#<<Parameters>>.foc_mbrad
  expr: Constraints[91] = <<Common>>#<<Parameters>>.foc_mbrad - <<Common>>#<<Parameters>>.foc_baseflange / 2 - <<Common>>#<<Parameters>>.sec_fthick - <<Common>>#<<Parameters>>.sec_sidebolt * 3
  expr: Constraints[98] = <<Common>>#<<Parameters>>.sec_sidebolt_lower_z - <<Common>>#<<Parameters>>.mirror_distance
  expr: Constraints[99] = <<Common>>#<<Parameters>>.sec_sidebolt_upper_z - <<Common>>#<<Parameters>>.mirror_distance
  expr: Constraints[9] = <<Common>>#<<Parameters>>.datum_sec_upperhub + <<Common>>#<<Parameters>>.sec_stalkheight - <<Common>>#<<Parameters>>.mirror_distance
  sketch-geometry (64):
    g0: LineSegment StartX=-100 StartY=81 StartZ=0 EndX=100 EndY=81 EndZ=0
    g1: LineSegment StartX=100 StartY=81 StartZ=0 EndX=100 EndY=-54 EndZ=0
    g2: LineSegment StartX=100 StartY=-54 StartZ=0 EndX=-100 EndY=-54 EndZ=0
    g3: LineSegment StartX=-100 StartY=-54 StartZ=0 EndX=-100 EndY=81 EndZ=0
    g4: Circle CenterX=0 CenterY=0 CenterZ=0 NormalX=0 NormalY=0 NormalZ=1 AngleXU=0 Radius=30
    g5: LineSegment StartX=0 StartY=0 StartZ=0 EndX=28.5788 EndY=-16.5 EndZ=0
    g6: LineSegment StartX=0 StartY=0 StartZ=0 EndX=-28.5788 EndY=-16.5 EndZ=0
    g7: Circle CenterX=0 CenterY=0 CenterZ=0 NormalX=0 NormalY=0 NormalZ=1 AngleXU=0 Radius=33
    g8: ArcOfCircle CenterX=0 CenterY=0 CenterZ=0 NormalX=0 NormalY=0 NormalZ=1 AngleXU=0 Radius=30 StartAngle=1.84073 EndAngle=3.39526
    g9: ArcOfCircle CenterX=0 CenterY=0 CenterZ=0 NormalX=0 NormalY=0 NormalZ=1 AngleXU=0 Radius=30 StartAngle=3.93512 EndAngle=5.48965
    g10: ArcOfCircle CenterX=0 CenterY=0 CenterZ=0 NormalX=0 NormalY=0 NormalZ=1 AngleXU=0 Radius=30 StartAngle=6.02952 EndAngle=7.58405
    g11: LineSegment StartX=-8 StartY=28.9137 StartZ=0 EndX=-8 EndY=33 EndZ=0
    g12: LineSegment StartX=8 StartY=28.9137 StartZ=0 EndX=8 EndY=33 EndZ=0
    g13: LineSegment StartX=29.04 StartY=-7.52863 StartZ=0 EndX=32.5788 EndY=-9.57179 EndZ=0
    g14: LineSegment StartX=21.04 StartY=-21.385 StartZ=0 EndX=24.5788 EndY=-23.4282 EndZ=0
    g15: LineSegment StartX=-21.04 StartY=-21.385 StartZ=0 EndX=-24.5788 EndY=-23.4282 EndZ=0
    g16: LineSegment StartX=-29.04 StartY=-7.52863 StartZ=0 EndX=-32.5788 EndY=-9.57179 EndZ=0
    g17: ArcOfCircle CenterX=-28.5788 CenterY=-16.5 CenterZ=0 NormalX=0 NormalY=0 NormalZ=1 AngleXU=0 Radius=8 StartAngle=2.09439 EndAngle=5.23599
    g18: ArcOfCircle CenterX=28.5788 CenterY=-16.5 CenterZ=0 NormalX=0 NormalY=0 NormalZ=1 AngleXU=0 Radius=8 StartAngle=4.18879 EndAngle=7.33039
    g19: ArcOfCircle CenterX=0 CenterY=33 CenterZ=0 NormalX=0 NormalY=0 NormalZ=1 AngleXU=0 Radius=8 StartAngle=6.28318 EndAngle=9.42478
    g20: GeomPoint X=0 Y=41 Z=0
    g21: ArcOfCircle CenterX=-74 CenterY=73 CenterZ=0 NormalX=0 NormalY=0 NormalZ=1 AngleXU=0 Radius=2.2 StartAngle=-9e-16 EndAngle=3.14159
    g22: ArcOfCircle CenterX=-74 CenterY=69 CenterZ=0 NormalX=0 NormalY=0 NormalZ=1 AngleXU=0 Radius=2.2 StartAngle=3.14159 EndAngle=6.28319
    g23: LineSegment StartX=-76.2 StartY=73 StartZ=0 EndX=-76.2 EndY=69 EndZ=0
    g24: LineSegment StartX=-71.8 StartY=73 StartZ=0 EndX=-71.8 EndY=69 EndZ=0
    g25: ArcOfCircle CenterX=74 CenterY=73 CenterZ=0 NormalX=0 NormalY=0 NormalZ=1 AngleXU=0 Radius=2.2 StartAngle=2e-15 EndAngle=3.14159
    g26: ArcOfCircle CenterX=74 CenterY=69 CenterZ=0 NormalX=0 NormalY=0 NormalZ=1 AngleXU=0 Radius=2.2 StartAngle=3.14159 EndAngle=6.28319
    g27: LineSegment StartX=71.8 StartY=73 StartZ=0 EndX=71.8 EndY=69 EndZ=0
    g28: LineSegment StartX=76.2 StartY=73 StartZ=0 EndX=76.2 EndY=69 EndZ=0
    g29: LineSegment StartX=71.8 StartY=73 StartZ=0 EndX=76.2 EndY=69 EndZ=0
    g30: LineSegment StartX=76.2 StartY=73 StartZ=0 EndX=71.8 EndY=69 EndZ=0
    g31: GeomPoint X=74 Y=71 Z=0
    g32: Circle CenterX=0 CenterY=-36 CenterZ=0 NormalX=0 NormalY=0 NormalZ=1 AngleXU=0 Radius=2.2
    g33: Circle CenterX=36 CenterY=15 CenterZ=0 NormalX=0 NormalY=0 NormalZ=1 AngleXU=0 Radius=2.2
    g34: Circle CenterX=-36 CenterY=15 CenterZ=0 NormalX=0 NormalY=0 NormalZ=1 AngleXU=0 Radius=2.2
    g35: LineSegment StartX=-76.2 StartY=73 StartZ=0 EndX=-71.8 EndY=69 EndZ=0
    g36: LineSegment StartX=-71.8 StartY=73 StartZ=0 EndX=-76.2 EndY=69 EndZ=0
    g37: GeomPoint X=-74 Y=71 Z=0
    g38: LineSegment StartX=100 StartY=71 StartZ=0 EndX=-100 EndY=71 EndZ=0
    g39: LineSegment StartX=-100 StartY=-44 StartZ=0 EndX=100 EndY=-44 EndZ=0
    g40: LineSegment StartX=74 StartY=81 StartZ=0 EndX=74 EndY=-54 EndZ=0
    g41: LineSegment StartX=90 StartY=81 StartZ=0 EndX=90 EndY=-54 EndZ=0
    g42: Circle CenterX=90 CenterY=-44 CenterZ=0 NormalX=0 NormalY=0 NormalZ=1 AngleXU=0 Radius=2.2
    g43: Circle CenterX=-90 CenterY=-44 CenterZ=0 NormalX=0 NormalY=0 NormalZ=1 AngleXU=0 Radius=2.2
    g44: ArcOfCircle CenterX=-90 CenterY=73 CenterZ=0 NormalX=0 NormalY=0 NormalZ=1 AngleXU=0 Radius=2.2 StartAngle=2.2e-15 EndAngle=3.14159
    g45: ArcOfCircle CenterX=-90 CenterY=69 CenterZ=0 NormalX=0 NormalY=0 NormalZ=1 AngleXU=0 Radius=2.2 StartAngle=3.14159 EndAngle=6.28319
    g46: LineSegment StartX=-92.2 StartY=73 StartZ=0 EndX=-92.2 EndY=69 EndZ=0
    g47: LineSegment StartX=-87.8 StartY=73 StartZ=0 EndX=-87.8 EndY=69 EndZ=0
    g48: ArcOfCircle CenterX=90 CenterY=73 CenterZ=0 NormalX=0 NormalY=0 NormalZ=1 AngleXU=0 Radius=2.2 StartAngle=2.7e-15 EndAngle=3.14159
    g49: ArcOfCircle CenterX=90 CenterY=69 CenterZ=0 NormalX=0 NormalY=0 NormalZ=1 AngleXU=0 Radius=2.2 StartAngle=3.14159 EndAngle=6.28319
    g50: LineSegment StartX=87.8 StartY=73 StartZ=0 EndX=87.8 EndY=69 EndZ=0
    g51: LineSegment StartX=92.2 StartY=73 StartZ=0 EndX=92.2 EndY=69 EndZ=0
    g52: LineSegment StartX=87.8 StartY=73 StartZ=0 EndX=92.2 EndY=69 EndZ=0
    g53: LineSegment StartX=92.2 StartY=73 StartZ=0 EndX=87.8 EndY=69 EndZ=0
    g54: GeomPoint X=90 Y=71 Z=0
    g55: LineSegment StartX=-92.2 StartY=73 StartZ=0 EndX=-87.8 EndY=69 EndZ=0
    g56: LineSegment StartX=-87.8 StartY=73 StartZ=0 EndX=-92.2 EndY=69 EndZ=0
    g57: GeomPoint X=-90 Y=71 Z=0
    g58: Circle CenterX=74 CenterY=-44 CenterZ=0 NormalX=0 NormalY=0 NormalZ=1 AngleXU=0 Radius=2.2
    g59: Circle CenterX=-74 CenterY=-44 CenterZ=0 NormalX=0 NormalY=0 NormalZ=1 AngleXU=0 Radius=2.2
    g60: Circle CenterX=90 CenterY=71 CenterZ=0 NormalX=0 NormalY=0 NormalZ=1 AngleXU=0 Radius=2.2
    g61: Circle CenterX=74 CenterY=71 CenterZ=0 NormalX=0 NormalY=0 NormalZ=1 AngleXU=0 Radius=2.2
    g62: Circle CenterX=-90 CenterY=71 CenterZ=0 NormalX=0 NormalY=0 NormalZ=1 AngleXU=0 Radius=2.2
    g63: Circle CenterX=-74 CenterY=71 CenterZ=0 NormalX=0 NormalY=0 NormalZ=1 AngleXU=0 Radius=2.2
  constraints (165):
    c: Coincident(g0,g1)
    c: Coincident(g1,g2)
    c: Coincident(g2,g3)
    c: Coincident(g3,g0)
    c: Horizontal(g0)
    c: Vertical(g1)
    c: Vertical(g3)
    c: Symmetric(g1,g2,g-2)
    c: DistanceX(g1) = 100
    c: DistanceY(g0) = 81
    c: Coincident(g4,g-1)
    c: Radius(g4) = 30
    c: DistanceY(g1,g-1) = 54
    c: Coincident(g5,g-1)
    c: Coincident(g6,g5)
    c: Symmetric(g5,g6,g-2)
    c: Angle(g6,g5) = 2.0944
    c: Coincident(g7,g-1)
    c: Radius(g7) = 33
    c: PointOnObject(g5,g7)
    c: PointOnObject(g9,g4)
    c: PointOnObject(g10,g4)
    c: Coincident(g8,g-1)
    c: Coincident(g9,g8)
    c: Coincident(g10,g8)
    c: PointOnObject(g8,g4)
    c: Coincident(g11,g8)
    c: Coincident(g12,g10)
    c: Coincident(g13,g10)
    c: Coincident(g14,g9)
    c: Coincident(g15,g9)
    c: Coincident(g16,g8)
    c: Vertical(g11)
    c: Vertical(g12)
    c: Parallel(g15,g16)
    c: Parallel(g16,g6)
    c: Parallel(g14,g13)
    c: Parallel(g13,g5)
    c: Coincident(g17,g6)
    c: Coincident(g17,g15)
    c: Coincident(g17,g16)
    c: Coincident(g18,g5)
    c: Coincident(g18,g14)
    c: Coincident(g18,g13)
    c: PointOnObject(g19,g7)
    c: Coincident(g19,g11)
    c: Coincident(g19,g12)
    c: PointOnObject(g19,g-2)
    c: Equal(g19,g17)
    c: Equal(g17,g18)
    c: DistanceX(g11,g12) = 16
    c: Equal(g12,g11)
    c: Equal(g11,g16)
    c: Equal(g16,g15)
    c: Equal(g15,g14)
    c: Equal(g14,g13)
    c: PointOnObject(g20,g19)
    c: PointOnObject(g20,g-2)
    c: DistanceY(g19,g20) = 8
    c: Tangent(g21,g24) = 1.5708
    c: Tangent(g21,g23) = -1.5708
    c: Tangent(g23,g22) = -1.5708
    c: Tangent(g24,g22) = 1.5708
    c: Vertical(g23)
    c: Equal(g21,g22)
    c: Tangent(g25,g28) = 1.5708
    c: Tangent(g25,g27) = -1.5708
    c: Tangent(g27,g26) = -1.5708
    c: Tangent(g28,g26) = 1.5708
    c: Vertical(g27)
    c: Equal(g25,g26)
    c: Coincident(g29,g25)
    c: Coincident(g29,g26)
    c: Coincident(g30,g25)
    c: Coincident(g30,g26)
    c: PointOnObject(g31,g29)
    c: PointOnObject(g31,g30)
    c: PointOnObject(g32,g-2)
    c: Diameter(g34) = 4.4
    c: Equal(g34,g33)
    c: Equal(g34,g32)
    c: Symmetric(g33,g34,g-2)
    c: Coincident(g35,g21)
    c: Coincident(g35,g22)
    c: Coincident(g36,g21)
    c: Coincident(g36,g22)
    c: PointOnObject(g37,g35)
    c: PointOnObject(g37,g36)
    c: Symmetric(g37,g31,g-2)
    c: DistanceX(g33) = 36
    c: DistanceY(g32,g-1) = 36
    c: DistanceY(g33) = 15
    c: PointOnObject(g38,g1)
    c: PointOnObject(g38,g3)
    c: Horizontal(g38)
    c: PointOnObject(g39,g3)
    c: PointOnObject(g39,g1)
    c: Horizontal(g39)
    c: DistanceY(g39) = -44
    c: DistanceY(g38) = 71
    c: PointOnObject(g40,g0)
    c: PointOnObject(g40,g2)
    c: Vertical(g40)
    c: PointOnObject(g41,g0)
    c: PointOnObject(g41,g2)
    c: Vertical(g41)
    c: DistanceX(g41) = 90
    c: DistanceX(g40,g41) = 16
    c: PointOnObject(g42,g41)
    c: Symmetric(g43,g42,g-2)
    c: PointOnObject(g42,g39)
    c: Diameter(g42) = 4.4
    c: Equal(g42,g43)
    c: PointOnObject(g31,g38)
    c: PointOnObject(g31,g40)
    c: Tangent(g44,g47) = 1.5708
    c: Tangent(g44,g46) = -1.5708
    c: Tangent(g46,g45) = -1.5708
    c: Tangent(g47,g45) = 1.5708
    c: Vertical(g46)
    c: Equal(g44,g45)
    c: Tangent(g48,g51) = 1.5708
    c: Tangent(g48,g50) = -1.5708
    c: Tangent(g50,g49) = -1.5708
    c: Tangent(g51,g49) = 1.5708
    c: Vertical(g50)
    c: Equal(g48,g49)
    c: Coincident(g52,g48)
    c: Coincident(g52,g49)
    c: Coincident(g53,g48)
    c: Coincident(g53,g49)
    c: PointOnObject(g54,g52)
    c: PointOnObject(g54,g53)
    c: PointOnObject(g54,g41)
    c: PointOnObject(g54,g38)
    c: Equal(g50,g28)
    c: Equal(g25,g48)
    c: Coincident(g55,g44)
    c: Coincident(g55,g45)
    c: Coincident(g56,g44)
    c: Coincident(g56,g45)
    c: PointOnObject(g57,g55)
    c: PointOnObject(g57,g56)
    c: Equal(g47,g24)
    c: Equal(g44,g21)
    c: Symmetric(g57,g54,g-2)
    c: PointOnObject(g58,g40)
    c: PointOnObject(g58,g39)
    c: Symmetric(g59,g58,g-2)
    c: Equal(g58,g59)
    c: Equal(g59,g22)
    c: Diameter(g58) = 4.4
    c: Equal(g49,g22)
    c: DistanceY(g46,g46) = 4
    c: Equal(g27,g24)
    c: Coincident(g60,g54)
    c: Coincident(g61,g31)
    c: Coincident(g62,g57)
    c: Coincident(g63,g37)
    c: Equal(g62,g63)
    c: Equal(g63,g61)
    c: Equal(g61,g60)
    c: Equal(g60,g42)
    c: DistanceY(g3,g3) = 135
    c: DistanceY(g1,g42) = 10
FEATURE [PartDesign::Pad] Pad012  label="FocuserPlate_Pad"
  Direction = (1,-2e-16,3e-16)
  Length = 1
  Length2 = 100
  Placement = pos=(0,0,0) rot=(0.57735,0.57735,0.57735;2.0944rad)
  Profile = -> Sketch078
  Type = 0
  expr: Length = <<Common>>#<<Parameters>>.sec_spthick
FEATURE [PartDesign::CoordinateSystem] Local_CS154  label="LCS_PlateMount_ZF"
  AttacherType = Attacher::AttachEngine3D
  AttachmentOffset = pos=(-90,71,0) rot=(0,0,1;3.14159rad)
  MapMode = 5
  Placement = pos=(-3.57e-14,-90,71) rot=(0.57735,-0.57735,0.57735;4.18879rad)
  Support = -> [YZ_Plane014]
  expr: .AttachmentOffset.Base.x = -<<Common>>#<<Parameters>>.sec_sidebolt_y
  expr: .AttachmentOffset.Base.y = <<Common>>#<<Parameters>>.sec_sidebolt_upper_z - <<Common>>#<<Parameters>>.mirror_distance
FEATURE [PartDesign::CoordinateSystem] Local_CS155  label="LCS_PlateMount_ZA"
  AttacherType = Attacher::AttachEngine3D
  AttachmentOffset = pos=(90,71,0) rot=(0,0,1;0rad)
  MapMode = 5
  Placement = pos=(4.2e-15,90,71) rot=(0.57735,0.57735,0.57735;2.0944rad)
  Support = -> [YZ_Plane014]
  expr: .AttachmentOffset.Base.x = <<Common>>#<<Parameters>>.sec_sidebolt_y
  expr: .AttachmentOffset.Base.y = <<Common>>#<<Parameters>>.sec_sidebolt_upper_z - <<Common>>#<<Parameters>>.mirror_distance
FEATURE [PartDesign::CoordinateSystem] Local_CS156  label="LCS_PlateMount_NF"
  AttacherType = Attacher::AttachEngine3D
  AttachmentOffset = pos=(-90,-44,0) rot=(0,0,1;3.14159rad)
  MapMode = 5
  Placement = pos=(-1.02e-14,-90,-44) rot=(0.57735,-0.57735,0.57735;4.18879rad)
  Support = -> [YZ_Plane014]
  expr: .AttachmentOffset.Base.x = -<<Common>>#<<Parameters>>.sec_sidebolt_y
  expr: .AttachmentOffset.Base.y = <<Common>>#<<Parameters>>.sec_sidebolt_lower_z - <<Common>>#<<Parameters>>.mirror_distance
FEATURE [PartDesign::CoordinateSystem] Local_CS157  label="LCS_PlateMount_NA"
  AttacherType = Attacher::AttachEngine3D
  AttachmentOffset = pos=(90,-44,0) rot=(0,0,1;0rad)
  MapMode = 5
  Placement = pos=(2.98e-14,90,-44) rot=(0.57735,0.57735,0.57735;2.0944rad)
  Support = -> [YZ_Plane014]
  expr: .AttachmentOffset.Base.x = <<Common>>#<<Parameters>>.sec_sidebolt_y
  expr: .AttachmentOffset.Base.y = <<Common>>#<<Parameters>>.sec_sidebolt_lower_z - <<Common>>#<<Parameters>>.mirror_distance
FEATURE [PartDesign::CoordinateSystem] Local_CS201  label="LCS_PlateBaseMount_N"
  AttacherType = Attacher::AttachEngine3D
  AttachmentOffset = pos=(0,-36,0) rot=(0,0,1;0rad)
  MapMode = 5
  Placement = pos=(8e-15,-8e-15,-36) rot=(0.57735,0.57735,0.57735;2.0944rad)
  Support = -> [YZ_Plane014]
  expr: .AttachmentOffset.Base.y = -<<Common>>#<<Parameters>>.foc_mbrad
FEATURE [PartDesign::CoordinateSystem] Local_CS205  label="LCS_PlateBaseMount_ZF"
  AttacherType = Attacher::AttachEngine3D
  AttachmentOffset = pos=(-36,15,0) rot=(0,0,1;0rad)
  MapMode = 5
  Placement = pos=(-1.13e-14,-36,15) rot=(0.57735,0.57735,0.57735;2.0944rad)
  Support = -> [YZ_Plane014]
  expr: .AttachmentOffset.Base.x = -<<Common>>#<<Parameters>>.foc_mbrad
  expr: .AttachmentOffset.Base.y = <<Common>>#<<Parameters>>.foc_mbrad - <<Common>>#<<Parameters>>.foc_baseflange / 2 - <<Common>>#<<Parameters>>.sec_fthick - <<Common>>#<<Parameters>>.sec_sidebolt * 3
FEATURE [PartDesign::CoordinateSystem] Local_CS206  label="LCS_PlateBaseMount_ZA"
  AttacherType = Attacher::AttachEngine3D
  AttachmentOffset = pos=(36,15,0) rot=(0,0,1;0rad)
  MapMode = 5
  Placement = pos=(4.7e-15,36,15) rot=(0.57735,0.57735,0.57735;2.0944rad)
  Support = -> [YZ_Plane014]
  expr: .AttachmentOffset.Base.x = <<Common>>#<<Parameters>>.foc_mbrad
  expr: .AttachmentOffset.Base.y = <<Common>>#<<Parameters>>.foc_mbrad - <<Common>>#<<Parameters>>.foc_baseflange / 2 - <<Common>>#<<Parameters>>.sec_fthick - <<Common>>#<<Parameters>>.sec_sidebolt * 3
FEATURE [Sketcher::SketchObject] Sketch114  label="FocuserPlate_MasterSketch"
  FullyConstrained = true
  MapMode = 5
  Placement = pos=(0,0,0) rot=(0.57735,0.57735,0.57735;2.0944rad)
  Support = -> [YZ_Plane014]
  expr: .Constraints.ShaftDia = <<Common>>#<<Parameters>>.foc_inner / 2 + <<Common>>#<<Parameters>>.foc_wall + <<Common>>#<<Parameters>>.foc_spacing
  expr: Constraints[15] = <<Common>>#<<Parameters>>.fbearing_outer
  expr: Constraints[39] = <<Common>>#<<Parameters>>.datum_sec_upperhub + <<Common>>#<<Parameters>>.sec_stalkheight - <<Common>>#<<Parameters>>.mirror_distance
  expr: Constraints[3] = .Constraints.ShaftDia + (<<Common>>#<<Parameters>>.fbearing_outer / 2 - <<Common>>#<<Parameters>>.foc_spacing) * 1 mm
  expr: Constraints[48] = <<Common>>#<<Parameters>>.sec_sidebolt_upper_z - <<Common>>#<<Parameters>>.mirror_distance
  expr: Constraints[49] = <<Common>>#<<Parameters>>.bolt_y - <<Common>>#<<Parameters>>.pri_poledia / 2 - <<Common>>#<<Parameters>>.sec_fthick
  expr: Constraints[50] = <<Common>>#<<Parameters>>.sec_sidebolt_y
  expr: Constraints[59] = <<Common>>#<<Parameters>>.sec_sidebolt_lower_z - <<Common>>#<<Parameters>>.mirror_distance - <<Common>>#<<Parameters>>.sec_clampheight / 2
  expr: Constraints[63] = <<Common>>#<<Parameters>>.sec_sidebolt_lower_z - <<Common>>#<<Parameters>>.mirror_distance
  sketch-geometry (25):
    g0: Circle CenterX=0 CenterY=0 CenterZ=0 NormalX=0 NormalY=0 NormalZ=1 AngleXU=0 Radius=30
    g1: Circle CenterX=0 CenterY=0 CenterZ=0 NormalX=0 NormalY=0 NormalZ=1 AngleXU=0 Radius=33
    g2: LineSegment StartX=0 StartY=33 StartZ=0 EndX=-28.5788 EndY=-16.5 EndZ=0
    g3: LineSegment StartX=-28.5788 StartY=-16.5 StartZ=0 EndX=28.5788 EndY=-16.5 EndZ=0
    g4: LineSegment StartX=28.5788 StartY=-16.5 StartZ=0 EndX=0 EndY=33 EndZ=0
    g5: Circle CenterX=0 CenterY=33 CenterZ=0 NormalX=0 NormalY=0 NormalZ=1 AngleXU=0 Radius=5
    g6: Circle CenterX=28.5788 CenterY=-16.5 CenterZ=0 NormalX=0 NormalY=0 NormalZ=1 AngleXU=0 Radius=5
    g7: Circle CenterX=-28.5788 CenterY=-16.5 CenterZ=0 NormalX=0 NormalY=0 NormalZ=1 AngleXU=0 Radius=5
    g8: LineSegment StartX=-57.1577 StartY=33 StartZ=0 EndX=57.1577 EndY=33 EndZ=0
    g9: LineSegment StartX=0 StartY=-66 StartZ=0 EndX=57.1577 EndY=33 EndZ=0
    g10: LineSegment StartX=0 StartY=-66 StartZ=0 EndX=-57.1577 EndY=33 EndZ=0
    g11: LineSegment StartX=-57.1577 StartY=33 StartZ=0 EndX=0 EndY=0 EndZ=0
    g12: LineSegment StartX=57.1577 StartY=33 StartZ=0 EndX=0 EndY=0 EndZ=0
    g13: LineSegment StartX=-100 StartY=81 StartZ=0 EndX=100 EndY=81 EndZ=0
    g14: LineSegment StartX=100 StartY=81 StartZ=0 EndX=100 EndY=-54 EndZ=0
    g15: LineSegment StartX=100 StartY=-54 StartZ=0 EndX=-100 EndY=-54 EndZ=0
    g16: LineSegment StartX=-100 StartY=-54 StartZ=0 EndX=-100 EndY=81 EndZ=0
    g17: LineSegment StartX=-100 StartY=71 StartZ=0 EndX=100 EndY=71 EndZ=0
    g18: LineSegment StartX=90 StartY=81 StartZ=0 EndX=90 EndY=-54 EndZ=0
    g19: LineSegment StartX=-90 StartY=81 StartZ=0 EndX=-90 EndY=-54 EndZ=0
    g20: Circle CenterX=-90 CenterY=71 CenterZ=0 NormalX=0 NormalY=0 NormalZ=1 AngleXU=0 Radius=2
    g21: Circle CenterX=90 CenterY=71 CenterZ=0 NormalX=0 NormalY=0 NormalZ=1 AngleXU=0 Radius=2
    g22: LineSegment StartX=100 StartY=-44 StartZ=0 EndX=-100 EndY=-44 EndZ=0
    g23: Circle CenterX=90 CenterY=-44 CenterZ=0 NormalX=0 NormalY=0 NormalZ=1 AngleXU=0 Radius=2
    g24: Circle CenterX=-90 CenterY=-44 CenterZ=0 NormalX=0 NormalY=0 NormalZ=1 AngleXU=0 Radius=2
  constraints (70):
    c: Coincident(g0,g-1)
    c: Radius(g0) = 30  'ShaftDia'
    c: Coincident(g1,g-1)
    c: Radius(g1) = 33
    c: PointOnObject(g2,g1)
    c: PointOnObject(g2,g1)
    c: Coincident(g3,g2)
    c: PointOnObject(g3,g1)
    c: Horizontal(g3)
    c: Coincident(g4,g3)
    c: Coincident(g4,g2)
    c: PointOnObject(g2,g-2)
    c: Angle(g2,g4) = 1.0472
    c: Coincident(g5,g2)
    c: Coincident(g7,g2)
    c: Diameter(g7) = 10
    c: Equal(g7,g6)
    c: Equal(g7,g5)
    c: Coincident(g6,g3)
    c: Horizontal(g8)
    c: PointOnObject(g10,g-2)
    c: PointOnObject(g2,g8)
    c: PointOnObject(g2,g10)
    c: PointOnObject(g3,g9)
    c: Coincident(g9,g10)
    c: Coincident(g9,g8)
    c: Coincident(g10,g8)
    c: Parallel(g9,g2)
    c: Coincident(g11,g8)
    c: Coincident(g11,g-1)
    c: Coincident(g12,g8)
    c: Coincident(g12,g-1)
    c: Coincident(g13,g14)
    c: Coincident(g14,g15)
    c: Coincident(g15,g16)
    c: Coincident(g16,g13)
    c: Horizontal(g15)
    c: Vertical(g14)
    c: Vertical(g16)
    c: DistanceY(g13) = 81
    c: PointOnObject(g17,g16)
    c: PointOnObject(g17,g14)
    c: Horizontal(g17)
    c: PointOnObject(g18,g13)
    c: PointOnObject(g18,g15)
    c: Vertical(g18)
    c: PointOnObject(g19,g15)
    c: Vertical(g19)
    c: DistanceY(g17) = 71
    c: DistanceX(g13) = 100
    c: DistanceX(g18) = 90
    c: Symmetric(g13,g13,g-2)
    c: Symmetric(g19,g18,g-2)
    c: PointOnObject(g20,g17)
    c: PointOnObject(g21,g17)
    c: PointOnObject(g21,g18)
    c: PointOnObject(g20,g19)
    c: Diameter(g20) = 4
    c: Equal(g20,g21)
    c: DistanceY(g14) = -54
    c: PointOnObject(g22,g14)
    c: PointOnObject(g22,g16)
    c: Horizontal(g22)
    c: DistanceY(g22) = -44
    c: PointOnObject(g23,g22)
    c: PointOnObject(g24,g22)
    c: PointOnObject(g24,g19)
    c: PointOnObject(g23,g18)
    c: Equal(g23,g24)
    c: Equal(g24,g21)
FEATURE [PartDesign::CoordinateSystem] Local_CS  label="LCS_MirrorSpacing"
  AttacherType = Attacher::AttachEngine3D
  AttachmentOffset = pos=(-121,0,0) rot=(0,0,1;0rad)
  MapMode = 5
  Placement = pos=(-121,0,0) rot=(0,0,1;0rad)
  Support = -> [XY_Plane014]
  expr: .AttachmentOffset.Base.x = -<<Common>>#<<Parameters>>.sec_focuserplate_x
FEATURE [PartDesign::Body] Body022005  label="FocuserPlate"
  Group = -> [Sketch078,Pad012,Local_CS154,Local_CS155,Local_CS156,Local_CS157,Local_CS201,Local_CS205,Local_CS206,Sketch114,Local_CS]
  Origin = -> Origin014
  Placement = pos=(121,0,835) rot=(0,0,1;0rad)
  Tip = -> Pad012
  expr: .Placement.Base.x = <<Common>>#<<Parameters>>.sec_focuserplate_x
  expr: .Placement.Base.z = <<Common>>#<<Parameters>>.mirror_distance
COMPONENT P4 — recipe-attached ("FBearingPad", modeled in this document).
Construction recipe (the document's own serialized feature program — sketch geometry with constraints, then the solid features built on it; lengths are millimeters unless a unit is written):

FEATURE [PartDesign::Plane] DatumPlane034  label="DatumPlane_FBearngPad_Axis"
  AttachmentOffset = pos=(6,0,0) rot=(1,0,0;1.0472rad)
  Length = 61.6877
  MapMode = 2
  Placement = pos=(6,0,0) rot=(1,0,0;1.0472rad)
  ResizeMode = 0
  Support = -> [XY_Plane076]
  Width = 79.989
  expr: .AttachmentOffset.Base.x = <<Common>>#<<Parameters>>.foc_fheight / 2
FEATURE [Sketcher::SketchObject] Sketch120  label="FBearingPad_Profile_Sketch"
  FullyConstrained = true
  MapMode = 5
  Placement = pos=(6,0,0) rot=(1,0,0;1.0472rad)
  Support = -> [DatumPlane034]
  expr: Constraints[0] = <<Common>>#<<Parameters>>.fbearing_outer + <<Common>>#<<Parameters>>.sec_fthick * 2 - 0.5
  expr: Constraints[10] = <<Common>>#<<Parameters>>.fbearing_tilt
  expr: Constraints[7] = <<Common>>#<<Parameters>>.sec_spthick
  expr: Constraints[9] = -<<Common>>#<<Parameters>>.foc_fheight / 2
  sketch-geometry (4):
    g0: LineSegment StartX=-6 StartY=7.75 StartZ=0 EndX=-6 EndY=-7.75 EndZ=0
    g1: LineSegment StartX=-6 StartY=7.75 StartZ=0 EndX=-7 EndY=7.75 EndZ=0
    g2: LineSegment StartX=-7 StartY=7.75 StartZ=0 EndX=-8.35607 EndY=-7.75 EndZ=0
    g3: LineSegment StartX=-8.35607 StartY=-7.75 StartZ=0 EndX=-6 EndY=-7.75 EndZ=0
  constraints (11):
    c: DistanceY(g0,g0) = 15.5
    c: Coincident(g1,g0)
    c: Horizontal(g1)
    c: Coincident(g2,g1)
    c: Coincident(g3,g2)
    c: Coincident(g3,g0)
    c: Horizontal(g3)
    c: DistanceX(g1,g1) = 1
    c: Symmetric(g0,g0,g-1)
    c: DistanceX(g0) = -6
    c: Angle(g2,g0) = 0.0872665
FEATURE [PartDesign::Pad] Pad040  label="FBearingPad_Profile_Pad"
  Direction = (0,-0.866025,0.5)
  Length = 42
  Length2 = 100
  Placement = pos=(6,0,0) rot=(1,0,0;1.0472rad)
  Profile = -> Sketch120
  Reversed = true
  Type = 0
  expr: Length = <<Common>>#<<Parameters>>.foc_inner / 2 + <<Common>>#<<Parameters>>.foc_wall + <<Common>>#<<Parameters>>.foc_spacing + <<Common>>#<<Parameters>>.foc_baseflange
FEATURE [PartDesign::Plane] DatumPlane035  label="DatumPlane_FBearingPad_Tilt"
  AttachmentOffset = pos=(0,0,0) rot=(0,-1,0;0.087266rad)
  Length = 86.4632
  MapMode = 4
  Placement = pos=(6,0,0) rot=(0.725486,0.178129,0.664786;2.75759rad)
  ResizeMode = 0
  Support = -> [DatumPlane034]
  Width = 82.3653
  expr: .AttachmentOffset.Rotation.Pitch = -<<Common>>#<<Parameters>>.fbearing_tilt
FEATURE [Sketcher::SketchObject] Sketch121  label="FBearingPad_Cutout_Sketch"
  FullyConstrained = true
  MapMode = 5
  Placement = pos=(0,0,0) rot=(0.57735,0.57735,0.57735;2.0944rad)
  Support = -> [YZ_Plane076]
  expr: Constraints[11] = <<Common>>#<<Parameters>>.fbearing_outer + <<Common>>#<<Parameters>>.sec_fthick * 2 - 0.5
  expr: Constraints[18] = <<Common>>#<<Parameters>>.fbearing_outer / 2 - <<Common>>#<<Parameters>>.foc_spacing
  expr: Constraints[5] = <<Common>>#<<Parameters>>.foc_inner / 2 + <<Common>>#<<Parameters>>.foc_wall + <<Common>>#<<Parameters>>.foc_spacing
  sketch-geometry (11):
    g0: ArcOfCircle CenterX=0 CenterY=0 CenterZ=0 NormalX=0 NormalY=0 NormalZ=1 AngleXU=0 Radius=30 StartAngle=5.49829 EndAngle=6.02088
    g1: ArcOfCircle CenterX=28.5788 CenterY=-16.5 CenterZ=0 NormalX=0 NormalY=0 NormalZ=1 AngleXU=0 Radius=7.75 StartAngle=4.18879 EndAngle=7.33038
    g2: LineSegment StartX=0 StartY=0 StartZ=0 EndX=28.5788 EndY=-16.5 EndZ=0
    g3: LineSegment StartX=28.9739 StartY=-7.77914 StartZ=0 EndX=32.4538 EndY=-9.7883 EndZ=0
    g4: LineSegment StartX=21.2239 StartY=-21.2025 StartZ=0 EndX=24.7038 EndY=-23.2117 EndZ=0
    g5: LineSegment StartX=32.4538 StartY=-9.7883 StartZ=0 EndX=24.7038 EndY=-23.2117 EndZ=0
    g6: GeomPoint X=25.9808 Y=-15 Z=0
    g7: LineSegment StartX=-9.71447 StartY=8.06677 StartZ=0 EndX=41.7355 EndY=8.06677 EndZ=0
    g8: LineSegment StartX=41.7355 StartY=8.06677 StartZ=0 EndX=41.7355 EndY=-33.1501 EndZ=0
    g9: LineSegment StartX=41.7355 StartY=-33.1501 StartZ=0 EndX=-9.71447 EndY=-33.1501 EndZ=0
    g10: LineSegment StartX=-9.71447 StartY=-33.1501 StartZ=0 EndX=-9.71447 EndY=8.06677 EndZ=0
  constraints (31):
    c: Coincident(g0,g-1)
    c: Coincident(g2,g0)
    c: Coincident(g3,g1)
    c: Coincident(g4,g1)
    c: Angle(g2) = -0.523599
    c: Radius(g0) = 30
    c: Parallel(g2,g3)
    c: Parallel(g4,g2)
    c: Coincident(g1,g2)
    c: Coincident(g3,g0)
    c: Coincident(g0,g4)
    c: Distance(g0,g0) = 15.5
    c: Coincident(g5,g1)
    c: Coincident(g5,g1)
    c: PointOnObject(g1,g5)
    c: Perpendicular(g3,g5)
    c: PointOnObject(g6,g2)
    c: PointOnObject(g6,g0)
    c: Distance(g6,g1) = 3
    c: Coincident(g7,g8)
    c: Coincident(g8,g9)
    c: Coincident(g9,g10)
    c: Coincident(g10,g7)
    c: Horizontal(g7)
    c: Horizontal(g9)
    c: Vertical(g8)
    c: Vertical(g10)
    c: DistanceX(g7) = -9.71447
    c: DistanceY(g7) = 8.06677
    c: DistanceX(g8) = 41.7355
    c: DistanceY(g8) = -33.1501
FEATURE [PartDesign::Pocket] Pocket061  label="FBearingPad_Cutout"
  BaseFeature = -> Pad040
  Direction = (-1,2e-16,-3e-16)
  Length = 5
  Length2 = 100
  Midplane = true
  Placement = pos=(6,0,0) rot=(1,0,0;1.0472rad)
  Profile = -> Sketch121
  Type = 1
FEATURE [Sketcher::SketchObject] Sketch122  label="FBearingPad_Shaft_Sketch"
  FullyConstrained = true
  MapMode = 5
  Placement = pos=(6,0,-2e-16) rot=(0.725486,0.178129,0.664786;2.75759rad)
  Support = -> [DatumPlane035]
  expr: Constraints[1] = <<Common>>#<<Parameters>>.foc_inner / 2 + <<Common>>#<<Parameters>>.foc_wall + <<Common>>#<<Parameters>>.fbearing_outer / 2
  expr: Constraints[2] = <<Common>>#<<Parameters>>.fbearing_inner
  sketch-geometry (1):
    g0: Circle CenterX=0 CenterY=-33 CenterZ=0 NormalX=0 NormalY=0 NormalZ=1 AngleXU=0 Radius=1.5
  constraints (3):
    c: PointOnObject(g0,g-2)
    c: DistanceY(g0,g-1) = 33
    c: Diameter(g0) = 3
FEATURE [PartDesign::Pocket] Pocket062  label="FBearingPad_Shaft"
  BaseFeature = -> Pocket061
  Direction = (-0.996195,0.0435779,0.0754791)
  Length = 5
  Length2 = 100
  Midplane = true
  Placement = pos=(6,0,0) rot=(1,0,0;1.0472rad)
  Profile = -> Sketch122
  Type = 1
FEATURE [PartDesign::Body] Body022023  label="FBearingPad"
  Group = -> [DatumPlane034,Sketch120,Pad040,DatumPlane035,Sketch121,Pocket061,Sketch122,Pocket062]
  Origin = -> Origin076
  Placement = pos=(123,0,835) rot=(0,0,1;0rad)
  Tip = -> Pocket062
  expr: .Placement.Base.x = <<Common>>#<<Parameters>>.bolt_x + <<Common>>#<<Parameters>>.sec_poledia / 2 + <<Common>>#<<Parameters>>.sec_spthick
  expr: .Placement.Base.z = <<Common>>#<<Parameters>>.mirror_distance
COMPONENT P5 — recipe-attached ("EyepieceAdaptor", modeled in this document).
Construction recipe (the document's own serialized feature program — sketch geometry with constraints, then the solid features built on it; lengths are millimeters unless a unit is written):

FEATURE [Sketcher::SketchObject] Sketch143  label="EyepieceAdaptor_Profile"
  FullyConstrained = true
  MapMode = 5
  Placement = pos=(0,0,0) rot=(1,0,0;1.5708rad)
  Support = -> [XZ_Plane082]
  expr: Constraints[13] = (31.7 + <<Common>>#<<Parameters>>.foc_itol) / 2
  expr: Constraints[14] = <<Common>>#<<Parameters>>.foc_wall + 1
  expr: Constraints[15] = <<Common>>#<<Parameters>>.foc_fheight
  expr: Constraints[16] = <<Common>>#<<Parameters>>.foc_flangeinner / 2
  expr: Constraints[17] = <<Common>>#<<Parameters>>.foc_fheight * 2
  expr: Constraints[23] = <<Common>>#<<Parameters>>.foc_flange - <<Common>>#<<Parameters>>.foc_fthick
  expr: Constraints[24] = <<Common>>#<<Parameters>>.foc_fthick
  sketch-geometry (9):
    g0: LineSegment StartX=0 StartY=25.4 StartZ=0 EndX=0 EndY=29.9 EndZ=0
    g1: LineSegment StartX=0 StartY=29.9 StartZ=0 EndX=0.5 EndY=29.9 EndZ=0
    g2: LineSegment StartX=2.5 StartY=27.9 StartZ=0 EndX=2.5 EndY=15.95 EndZ=0
    g3: LineSegment StartX=2.5 StartY=15.95 StartZ=0 EndX=-12 EndY=15.95 EndZ=0
    g4: LineSegment StartX=-12 StartY=15.95 StartZ=0 EndX=-12 EndY=22.4 EndZ=0
    g5: LineSegment StartX=-12 StartY=22.4 StartZ=0 EndX=-24 EndY=22.4 EndZ=0
    g6: LineSegment StartX=-24 StartY=22.4 StartZ=0 EndX=-24 EndY=25.4 EndZ=0
    g7: LineSegment StartX=-24 StartY=25.4 StartZ=0 EndX=0 EndY=25.4 EndZ=0
    g8: ArcOfCircle CenterX=0.5 CenterY=27.9 CenterZ=0 NormalX=0 NormalY=0 NormalZ=1 AngleXU=0 Radius=2 StartAngle=1.94069e-11 EndAngle=1.5708
  constraints (26):
    c: PointOnObject(g0,g-2)
    c: PointOnObject(g0,g-2)
    c: Coincident(g1,g0)
    c: Horizontal(g1)
    c: Vertical(g2)
    c: Coincident(g3,g2)
    c: Horizontal(g3)
    c: Coincident(g4,g3)
    c: Vertical(g4)
    c: Coincident(g5,g4)
    c: Horizontal(g5)
    c: Coincident(g6,g5)
    c: Vertical(g6)
    c: DistanceY(g2) = 15.95
    c: DistanceY(g6,g6) = 3
    c: DistanceX(g4,g0) = 12
    c: DistanceY(g6) = 25.4
    c: DistanceX(g6,g0) = 24
    c: Coincident(g7,g6)
    c: Horizontal(g7)
    c: Coincident(g0,g7)
    c: Tangent(g1,g8) = 1.5708
    c: Tangent(g2,g8) = 1.5708
    c: DistanceY(g0,g0) = 4.5
    c: DistanceX(g0,g2) = 2.5
    c: Radius(g8) = 2
FEATURE [PartDesign::Revolution] Revolution004  label="EyepieceAdaptor_Base"
  Angle = 360
  Axis = (1,0,0)
  Base = (0,0,0)
  Placement = pos=(0,0,0) rot=(1,0,0;1.5708rad)
  Profile = -> Sketch143
  ReferenceAxis = -> X_Axis082
FEATURE [PartDesign::Plane] DatumPlane037  label="DatumPlane_EyepieceAdaptor_Midpoint"
  AttachmentOffset = pos=(-6,0,0) rot=(1,0,0;2.0944rad)
  Length = 62.7676
  MapMode = 5
  Placement = pos=(-6,0,0) rot=(1,0,0;3.66519rad)
  ResizeMode = 0
  Support = -> [XZ_Plane082]
  Width = 94.2727
  expr: .AttachmentOffset.Base.x = -<<Common>>#<<Parameters>>.foc_fheight / 2
FEATURE [Sketcher::SketchObject] Sketch144  label="EyepieceAdaptor_ClampShaft_Sketch"
  FullyConstrained = true
  MapMode = 5
  Placement = pos=(-6,0,0) rot=(1,0,0;3.66519rad)
  Support = -> [DatumPlane037]
  sketch-geometry (1):
    g0: Circle CenterX=0 CenterY=0 CenterZ=0 NormalX=0 NormalY=0 NormalZ=1 AngleXU=0 Radius=2.2
  constraints (2):
    c: Coincident(g0,g-1)
    c: Diameter(g0) = 4.4
FEATURE [Sketcher::SketchObject] Sketch145  label="EyepieceAdaptor_ClampNut_Sketch"
  AttachmentOffset = pos=(0,0,25.4) rot=(0,0,1;0rad)
  FullyConstrained = true
  MapMode = 5
  Placement = pos=(-6,-12.7,21.997) rot=(0,-0.258819,0.965926;3.14159rad)
  Support = -> [DatumPlane037]
  expr: .AttachmentOffset.Base.z = <<Common>>#<<Parameters>>.foc_flangeinner / 2
  expr: Constraints[1] = <<Common>>#<<Parameters>>.acc_M4Bore
  sketch-geometry (1):
    g0: Circle CenterX=0 CenterY=0 CenterZ=0 NormalX=0 NormalY=0 NormalZ=1 AngleXU=0 Radius=2.8
  constraints (2):
    c: Coincident(g0,g-1)
    c: Diameter(g0) = 5.6
FEATURE [PartDesign::Plane] DatumPlane039  label="DatumPlane_EyepieceAdaptor_InnerPoint"
  AttachmentOffset = pos=(0,0,24) rot=(0,0,1;0rad)
  Length = 71.5273
  MapMode = 5
  Placement = pos=(-24,5.3e-15,-5.3e-15) rot=(-0.57735,0.57735,0.57735;4.18879rad)
  ResizeMode = 0
  Support = -> [YZ_Plane082]
  Width = 71.7388
  expr: .AttachmentOffset.Base.z = <<Common>>#<<Parameters>>.foc_fheight * 2
FEATURE [Sketcher::SketchObject] Sketch147  label="EyepieceAdaptor_SideCut_Sketch"
  FullyConstrained = true
  MapMode = 5
  Placement = pos=(-24,5.3e-15,-5.3e-15) rot=(-0.57735,0.57735,0.57735;4.18879rad)
  Support = -> [DatumPlane039]
  expr: Constraints[14] = <<Common>>#<<Parameters>>.foc_fthick - <<Common>>#<<Parameters>>.foc_itol
  expr: Constraints[15] = <<Common>>#<<Parameters>>.foc_fthick * 2 - <<Common>>#<<Parameters>>.foc_itol * 2
  expr: Constraints[1] = <<Common>>#<<Parameters>>.foc_flangeinner
  expr: Constraints[6] = <<Common>>#<<Parameters>>.foc_flangeinner + <<Common>>#<<Parameters>>.foc_flange * 2
  sketch-geometry (6):
    g0: ArcOfCircle CenterX=0 CenterY=0 CenterZ=0 NormalX=0 NormalY=0 NormalZ=1 AngleXU=0 Radius=25.4 StartAngle=1.13787 EndAngle=7.23971
    g1: LineSegment StartX=0 StartY=0 StartZ=0 EndX=12.7 EndY=21.997 EndZ=0
    g2: Circle CenterX=0 CenterY=0 CenterZ=0 NormalX=0 NormalY=0 NormalZ=1 AngleXU=0 Radius=32.4
    g3: LineSegment StartX=10.656 StartY=23.0567 StartZ=0 EndX=11.806 EndY=25.0485 EndZ=0
    g4: LineSegment StartX=11.806 StartY=25.0485 StartZ=0 EndX=15.7897 EndY=22.7485 EndZ=0
    g5: LineSegment StartX=15.7897 StartY=22.7485 StartZ=0 EndX=14.6397 EndY=20.7567 EndZ=0
  constraints (16):
    c: Coincident(g0,g-1)
    c: Diameter(g0) = 50.8
    c: Coincident(g1,g0)
    c: PointOnObject(g1,g0)
    c: Angle(g-1,g1) = 1.0472
    c: Coincident(g2,g0)
    c: Diameter(g2) = 64.8
    c: Coincident(g3,g0)
    c: Coincident(g4,g3)
    c: Coincident(g5,g4)
    c: Coincident(g5,g0)
    c: Symmetric(g4,g3,g1)
    c: Parallel(g5,g1)
    c: Parallel(g3,g1)
    c: Distance(g3) = 2.3
    c: Distance(g4) = 4.6
FEATURE [Sketcher::SketchObject] Sketch148  label="EyepieceAdaptor_ClampPad_Sketch"
  AttachmentOffset = pos=(0,0,-25.05) rot=(0,0,1;0rad)
  FullyConstrained = true
  MapMode = 5
  Placement = pos=(-6,-12.525,21.6939) rot=(1,0,0;3.66519rad)
  Support = -> [DatumPlane037]
  expr: .AttachmentOffset.Base.z = -(<<Common>>#<<Parameters>>.foc_itol + 31.7 / 2 + 9)
  sketch-geometry (1):
    g0: Circle CenterX=0 CenterY=0 CenterZ=0 NormalX=0 NormalY=0 NormalZ=1 AngleXU=0 Radius=4.5
  constraints (2):
    c: Coincident(g0,g-1)
    c: Diameter(g0) = 9
FEATURE [PartDesign::CoordinateSystem] Local_CS230  label="LCS_AdaptorRoot"
  AttacherType = Attacher::AttachEngine3D
  MapMode = 11
  Placement = pos=(0,0,0) rot=(0.57735,-0.57735,0.57735;4.18879rad)
  Support = -> [Revolution004]
FEATURE [PartDesign::Hole] Hole050  label="EyepieceAdaptor_ClampShaft"
  BaseFeature = -> Revolution004
  CustomThreadClearance = 0
  Depth = 179.022
  DepthType = 1
  Diameter = 4.5
  DrillForDepth = false
  DrillPoint = 1
  DrillPointAngle = 118
  HoleCutCountersinkAngle = 90
  HoleCutCustomValues = false
  HoleCutDepth = 0
  HoleCutDiameter = 6.1
  HoleCutType = 0
  ModelThread = false
  Placement = pos=(0,0,0) rot=(1,0,0;1.5708rad)
  Profile = -> Sketch144
  Tapered = false
  TaperedAngle = 90
  ThreadClass = 0
  ThreadDepth = 23.5
  ThreadDepthType = 0
  ThreadDirection = 0
  ThreadFit = 0
  ThreadSize = 11
  ThreadType = 1
  Threaded = false
  UseCustomThreadClearance = false
FEATURE [PartDesign::Pocket] Pocket198  label="EyepieceAdaptor_ClampNut"
  BaseFeature = -> Hole050
  Direction = (0,0.5,-0.866025)
  Length = 4.5
  Length2 = 5
  Placement = pos=(0,0,0) rot=(1,0,0;1.5708rad)
  Profile = -> Sketch145
  ReferenceAxis = -> Sketch145 [N_Axis]
  Type = 0
FEATURE [PartDesign::CoordinateSystem] Local_CS231  label="LCS_AdaptorNut"
  AttacherType = Attacher::AttachEngine3D
  AttachmentOffset = pos=(0,0,4) rot=(0,0,1;0rad)
  MapMode = 11
  Placement = pos=(-6,-12.45,21.564) rot=(0.250563,0.250563,-0.935113;1.63783rad)
  Support = -> [Pocket198]
FEATURE [PartDesign::CoordinateSystem] Local_CS232  label="LCS_AdaptorScrew"
  AttacherType = Attacher::AttachEngine3D
  AttachmentOffset = pos=(0,0,12) rot=(0,0,1;0rad)
  MapMode = 11
  Placement = pos=(-6,-16.45,28.4922) rot=(0.250563,0.250563,-0.935113;1.63783rad)
  Support = -> [Pocket198]
FEATURE [PartDesign::Chamfer] Chamfer002  label="EyepieceAdaptor_RimChamfer"
  Angle = 45
  Base = -> Pocket198 [Edge2]
  BaseFeature = -> Pocket198
  ChamferType = 0
  FlipDirection = false
  Placement = pos=(0,0,0) rot=(1,0,0;1.5708rad)
  Size = 0.6
  Size2 = 1
  SupportTransform = false
  UseAllEdges = false
FEATURE [PartDesign::Body] Body022029  label="EyepieceAdaptor"
  Group = -> [Sketch143,Revolution004,Sketch144,DatumPlane037,Sketch145,DatumPlane039,Sketch147,Sketch148,Local_CS230,Local_CS231,Local_CS232,Hole050,Pocket198,Chamfer002]
  Origin = -> Origin082
  Placement = pos=(194,0,835) rot=(0,0,1;0rad)
  Tip = -> Chamfer002
  expr: .Placement.Base.x = <<Common>>#<<Parameters>>.bolt_x + <<Common>>#<<Parameters>>.sec_poledia / 2 + <<Common>>#<<Parameters>>.foc_shaft
  expr: .Placement.Base.z = <<Common>>#<<Parameters>>.mirror_distance
PROVENANCE & LICENSES
A FreeCAD (.FCStd) document from a public repository crawl; recipes are the document's own serialized feature recipes (and, for linked parts, companion documents' recipes).
License: as declared in the source repository (recorded in the dataset sidecar).
